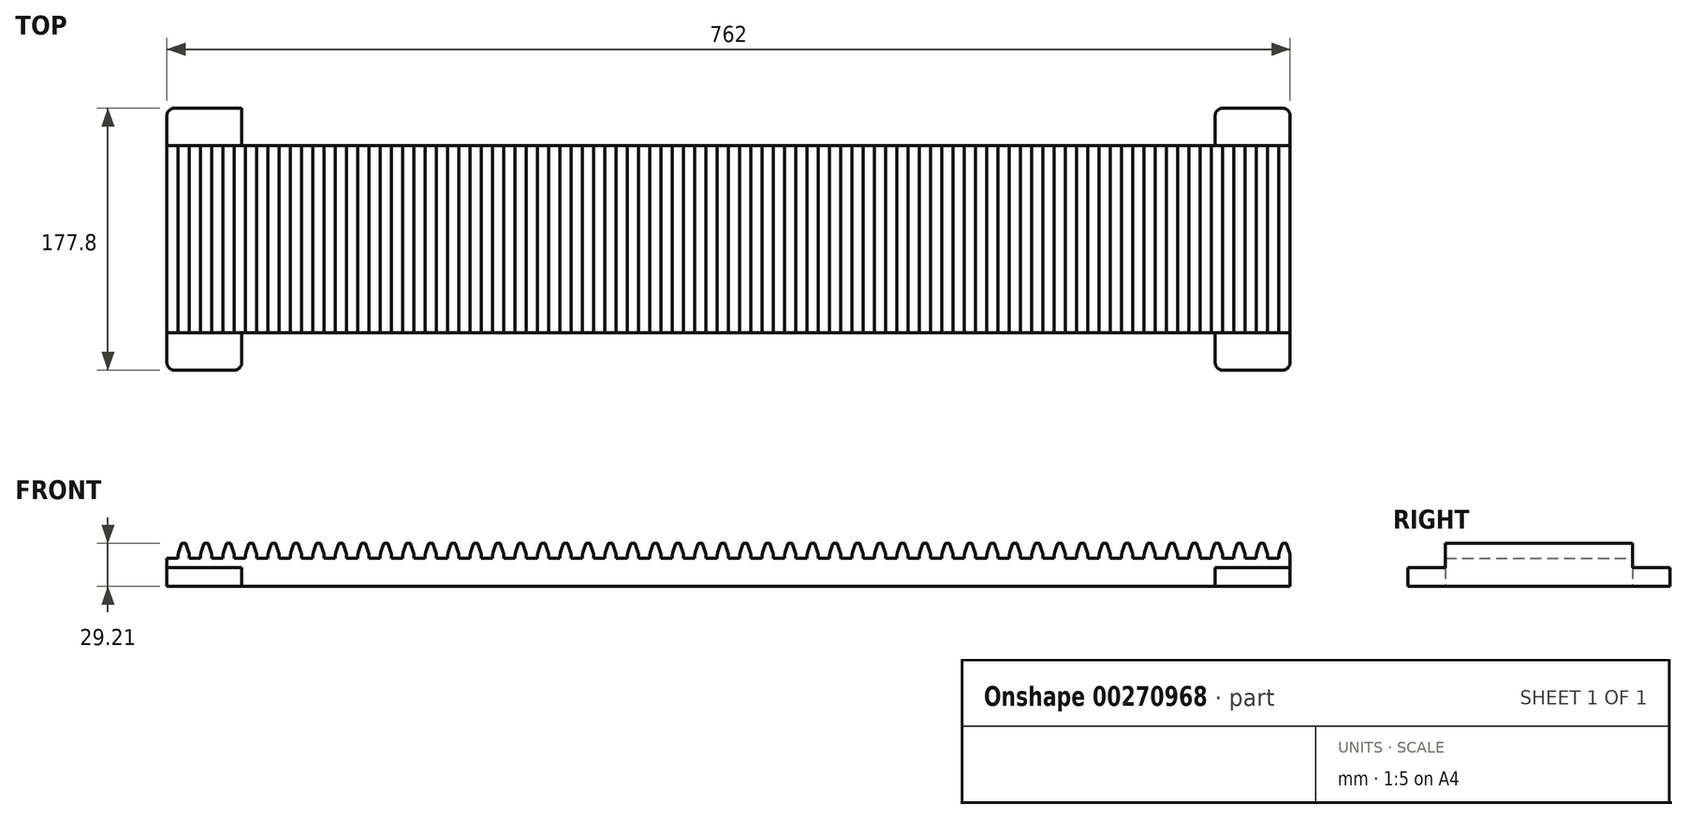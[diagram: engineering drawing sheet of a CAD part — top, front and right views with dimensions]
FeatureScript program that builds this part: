
annotation { "Feature Type Name" : "Feature", "Feature Type Description" : "" }
export const myFeature = defineFeature(function(context is Context, id is Id, definition is map)
    precondition{}
    {
        {
            var Q0;
            Q0=qCreatedBy(makeId("Front.planeOp"),FACE);
            var sketch = newSketch(context, id + "F0", { "sketchPlane" : qUnion([Q0])});
            skLineSegment(sketch, "E0", {"start": v(0, 0) * mm, "end": v(0, -19.05) * mm});
            skLineSegment(sketch, "E1", {"start": v(0, -19.05) * mm, "end": v(762, -19.05) * mm});
            skLineSegment(sketch, "E2", {"start": v(762, -19.05) * mm, "end": v(762, 0) * mm});
            skLineSegment(sketch, "E3", {"start": v(762, 0) * mm, "end": v(0, 0) * mm});
            skLineSegment(sketch, "E4", {"start": v(0, 0) * mm, "end": v(7.62, 0) * mm});
            skLineSegment(sketch, "E5", {"start": v(7.62, 0) * mm, "end": v(7.62, 1.79) * mm});
            skLineSegment(sketch, "E6", {"start": v(10.53, 10.16) * mm, "end": v(12.33, 10.16) * mm});
            skLineSegment(sketch, "E7", {"start": v(15.24, 1.79) * mm, "end": v(15.24, 0) * mm});
            skLineSegment(sketch, "E8", {"start": v(9.78, 9.6) * mm, "end": v(7.92, 3.7) * mm});
            skLineSegment(sketch, "E9", {"start": v(13.08, 9.6) * mm, "end": v(14.94, 3.7) * mm});
            skPoint(sketch, "E10.visualSharp", {"position": v(7.62, 2.77) * mm});
            skArc(sketch, "E10.filletArc", {"start": v(7.92, 3.7) * mm, "mid": v(7.7, 2.76) * mm, "end": v(7.62, 1.79) * mm});
            skPoint(sketch, "E11.visualSharp", {"position": v(15.24, 2.77) * mm});
            skArc(sketch, "E11.filletArc", {"start": v(15.24, 1.79) * mm, "mid": v(15.17, 2.76) * mm, "end": v(14.94, 3.7) * mm});
            skPoint(sketch, "E12.visualSharp", {"position": v(12.9, 10.16) * mm});
            skArc(sketch, "E12.filletArc", {"start": v(13.08, 9.6) * mm, "mid": v(12.8, 10) * mm, "end": v(12.33, 10.16) * mm});
            skPoint(sketch, "E13.visualSharp", {"position": v(9.96, 10.16) * mm});
            skArc(sketch, "E13.filletArc", {"start": v(10.53, 10.16) * mm, "mid": v(10.07, 10) * mm, "end": v(9.78, 9.6) * mm});
            skLineSegment(sketch, "E14", {"start": v(15.24, 0) * mm, "end": v(22.86, 0) * mm});
            skLineSegment(sketch, "E15.1.0.0", {"start": v(22.86, 0) * mm, "end": v(22.86, 1.79) * mm});
            skArc(sketch, "E15.1.0.1", {"start": v(23.16, 3.7) * mm, "mid": v(22.93, 2.76) * mm, "end": v(22.86, 1.79) * mm});
            skLineSegment(sketch, "E15.1.0.2", {"start": v(25.02, 9.6) * mm, "end": v(23.16, 3.7) * mm});
            skArc(sketch, "E15.1.0.3", {"start": v(25.77, 10.16) * mm, "mid": v(25.3, 10) * mm, "end": v(25.02, 9.6) * mm});
            skLineSegment(sketch, "E15.1.0.4", {"start": v(25.77, 10.16) * mm, "end": v(27.57, 10.16) * mm});
            skArc(sketch, "E15.1.0.5", {"start": v(28.32, 9.6) * mm, "mid": v(28.03, 10) * mm, "end": v(27.57, 10.16) * mm});
            skLineSegment(sketch, "E15.1.0.6", {"start": v(28.32, 9.6) * mm, "end": v(30.18, 3.7) * mm});
            skArc(sketch, "E15.1.0.7", {"start": v(30.48, 1.79) * mm, "mid": v(30.4, 2.76) * mm, "end": v(30.18, 3.7) * mm});
            skLineSegment(sketch, "E15.1.0.8", {"start": v(30.48, 1.79) * mm, "end": v(30.48, 0) * mm});
            skLineSegment(sketch, "E15.2.0.0", {"start": v(38.1, 0) * mm, "end": v(38.1, 1.79) * mm});
            skArc(sketch, "E15.2.0.1", {"start": v(38.4, 3.7) * mm, "mid": v(38.17, 2.76) * mm, "end": v(38.1, 1.79) * mm});
            skLineSegment(sketch, "E15.2.0.2", {"start": v(40.26, 9.6) * mm, "end": v(38.4, 3.7) * mm});
            skArc(sketch, "E15.2.0.3", {"start": v(41.01, 10.16) * mm, "mid": v(40.55, 10) * mm, "end": v(40.26, 9.6) * mm});
            skLineSegment(sketch, "E15.2.0.4", {"start": v(41.01, 10.16) * mm, "end": v(42.8, 10.16) * mm});
            skArc(sketch, "E15.2.0.5", {"start": v(43.56, 9.6) * mm, "mid": v(43.27, 10) * mm, "end": v(42.8, 10.16) * mm});
            skLineSegment(sketch, "E15.2.0.6", {"start": v(43.56, 9.6) * mm, "end": v(45.42, 3.7) * mm});
            skArc(sketch, "E15.2.0.7", {"start": v(45.72, 1.79) * mm, "mid": v(45.65, 2.76) * mm, "end": v(45.42, 3.7) * mm});
            skLineSegment(sketch, "E15.2.0.8", {"start": v(45.72, 1.79) * mm, "end": v(45.72, 0) * mm});
            skLineSegment(sketch, "E15.direction1", {"start": v(7.62, 0) * mm, "end": v(22.86, 0) * mm, "construction": true});
            skLineSegment(sketch, "E16.0.3.0", {"start": v(53.34, 0) * mm, "end": v(53.34, 1.79) * mm});
            skArc(sketch, "E16.3.3.0", {"start": v(53.64, 3.7) * mm, "mid": v(53.41, 2.76) * mm, "end": v(53.34, 1.79) * mm});
            skLineSegment(sketch, "E16.7.3.0", {"start": v(55.5, 9.6) * mm, "end": v(53.64, 3.7) * mm});
            skArc(sketch, "E16.10.3.0", {"start": v(56.25, 10.16) * mm, "mid": v(55.79, 10) * mm, "end": v(55.5, 9.6) * mm});
            skLineSegment(sketch, "E16.14.3.0", {"start": v(56.25, 10.16) * mm, "end": v(58.05, 10.16) * mm});
            skArc(sketch, "E16.17.3.0", {"start": v(58.8, 9.6) * mm, "mid": v(58.51, 10) * mm, "end": v(58.05, 10.16) * mm});
            skLineSegment(sketch, "E16.21.3.0", {"start": v(58.8, 9.6) * mm, "end": v(60.66, 3.7) * mm});
            skArc(sketch, "E16.24.3.0", {"start": v(60.96, 1.79) * mm, "mid": v(60.89, 2.76) * mm, "end": v(60.66, 3.7) * mm});
            skLineSegment(sketch, "E16.28.3.0", {"start": v(60.96, 1.79) * mm, "end": v(60.96, 0) * mm});
            skLineSegment(sketch, "E16.0.4.0", {"start": v(68.58, 0) * mm, "end": v(68.58, 1.79) * mm});
            skArc(sketch, "E16.3.4.0", {"start": v(68.88, 3.7) * mm, "mid": v(68.65, 2.76) * mm, "end": v(68.58, 1.79) * mm});
            skLineSegment(sketch, "E16.7.4.0", {"start": v(70.74, 9.6) * mm, "end": v(68.88, 3.7) * mm});
            skArc(sketch, "E16.10.4.0", {"start": v(71.5, 10.16) * mm, "mid": v(71.03, 10) * mm, "end": v(70.74, 9.6) * mm});
            skLineSegment(sketch, "E16.14.4.0", {"start": v(71.5, 10.16) * mm, "end": v(73.29, 10.16) * mm});
            skArc(sketch, "E16.17.4.0", {"start": v(74.04, 9.6) * mm, "mid": v(73.75, 10) * mm, "end": v(73.29, 10.16) * mm});
            skLineSegment(sketch, "E16.21.4.0", {"start": v(74.04, 9.6) * mm, "end": v(75.9, 3.7) * mm});
            skArc(sketch, "E16.24.4.0", {"start": v(76.2, 1.79) * mm, "mid": v(76.13, 2.76) * mm, "end": v(75.9, 3.7) * mm});
            skLineSegment(sketch, "E16.28.4.0", {"start": v(76.2, 1.79) * mm, "end": v(76.2, 0) * mm});
            skLineSegment(sketch, "E16.0.5.0", {"start": v(83.82, 0) * mm, "end": v(83.82, 1.79) * mm});
            skArc(sketch, "E16.3.5.0", {"start": v(84.12, 3.7) * mm, "mid": v(83.9, 2.76) * mm, "end": v(83.82, 1.79) * mm});
            skLineSegment(sketch, "E16.7.5.0", {"start": v(85.98, 9.6) * mm, "end": v(84.12, 3.7) * mm});
            skArc(sketch, "E16.10.5.0", {"start": v(86.73, 10.16) * mm, "mid": v(86.27, 10) * mm, "end": v(85.98, 9.6) * mm});
            skLineSegment(sketch, "E16.14.5.0", {"start": v(86.73, 10.16) * mm, "end": v(88.53, 10.16) * mm});
            skArc(sketch, "E16.17.5.0", {"start": v(89.28, 9.6) * mm, "mid": v(89, 10) * mm, "end": v(88.53, 10.16) * mm});
            skLineSegment(sketch, "E16.21.5.0", {"start": v(89.28, 9.6) * mm, "end": v(91.14, 3.7) * mm});
            skArc(sketch, "E16.24.5.0", {"start": v(91.44, 1.79) * mm, "mid": v(91.37, 2.76) * mm, "end": v(91.14, 3.7) * mm});
            skLineSegment(sketch, "E16.28.5.0", {"start": v(91.44, 1.79) * mm, "end": v(91.44, 0) * mm});
            skLineSegment(sketch, "E16.0.6.0", {"start": v(99.06, 0) * mm, "end": v(99.06, 1.79) * mm});
            skArc(sketch, "E16.3.6.0", {"start": v(99.36, 3.7) * mm, "mid": v(99.13, 2.76) * mm, "end": v(99.06, 1.79) * mm});
            skLineSegment(sketch, "E16.7.6.0", {"start": v(101.22, 9.6) * mm, "end": v(99.36, 3.7) * mm});
            skArc(sketch, "E16.10.6.0", {"start": v(101.97, 10.16) * mm, "mid": v(101.5, 10) * mm, "end": v(101.22, 9.6) * mm});
            skLineSegment(sketch, "E16.14.6.0", {"start": v(101.97, 10.16) * mm, "end": v(103.77, 10.16) * mm});
            skArc(sketch, "E16.17.6.0", {"start": v(104.52, 9.6) * mm, "mid": v(104.23, 10) * mm, "end": v(103.77, 10.16) * mm});
            skLineSegment(sketch, "E16.21.6.0", {"start": v(104.52, 9.6) * mm, "end": v(106.38, 3.7) * mm});
            skArc(sketch, "E16.24.6.0", {"start": v(106.68, 1.79) * mm, "mid": v(106.6, 2.76) * mm, "end": v(106.38, 3.7) * mm});
            skLineSegment(sketch, "E16.28.6.0", {"start": v(106.68, 1.79) * mm, "end": v(106.68, 0) * mm});
            skLineSegment(sketch, "E16.0.7.0", {"start": v(114.3, 0) * mm, "end": v(114.3, 1.79) * mm});
            skArc(sketch, "E16.3.7.0", {"start": v(114.6, 3.7) * mm, "mid": v(114.37, 2.76) * mm, "end": v(114.3, 1.79) * mm});
            skLineSegment(sketch, "E16.7.7.0", {"start": v(116.46, 9.6) * mm, "end": v(114.6, 3.7) * mm});
            skArc(sketch, "E16.10.7.0", {"start": v(117.21, 10.16) * mm, "mid": v(116.75, 10) * mm, "end": v(116.46, 9.6) * mm});
            skLineSegment(sketch, "E16.14.7.0", {"start": v(117.21, 10.16) * mm, "end": v(119, 10.16) * mm});
            skArc(sketch, "E16.17.7.0", {"start": v(119.76, 9.6) * mm, "mid": v(119.47, 10) * mm, "end": v(119, 10.16) * mm});
            skLineSegment(sketch, "E16.21.7.0", {"start": v(119.76, 9.6) * mm, "end": v(121.62, 3.7) * mm});
            skArc(sketch, "E16.24.7.0", {"start": v(121.92, 1.79) * mm, "mid": v(121.85, 2.76) * mm, "end": v(121.62, 3.7) * mm});
            skLineSegment(sketch, "E16.28.7.0", {"start": v(121.92, 1.79) * mm, "end": v(121.92, 0) * mm});
            skLineSegment(sketch, "E16.0.8.0", {"start": v(129.54, 0) * mm, "end": v(129.54, 1.79) * mm});
            skArc(sketch, "E16.3.8.0", {"start": v(129.84, 3.7) * mm, "mid": v(129.61, 2.76) * mm, "end": v(129.54, 1.79) * mm});
            skLineSegment(sketch, "E16.7.8.0", {"start": v(131.7, 9.6) * mm, "end": v(129.84, 3.7) * mm});
            skArc(sketch, "E16.10.8.0", {"start": v(132.45, 10.16) * mm, "mid": v(131.99, 10) * mm, "end": v(131.7, 9.6) * mm});
            skLineSegment(sketch, "E16.14.8.0", {"start": v(132.45, 10.16) * mm, "end": v(134.25, 10.16) * mm});
            skArc(sketch, "E16.17.8.0", {"start": v(135, 9.6) * mm, "mid": v(134.71, 10) * mm, "end": v(134.25, 10.16) * mm});
            skLineSegment(sketch, "E16.21.8.0", {"start": v(135, 9.6) * mm, "end": v(136.86, 3.7) * mm});
            skArc(sketch, "E16.24.8.0", {"start": v(137.16, 1.79) * mm, "mid": v(137.09, 2.76) * mm, "end": v(136.86, 3.7) * mm});
            skLineSegment(sketch, "E16.28.8.0", {"start": v(137.16, 1.79) * mm, "end": v(137.16, 0) * mm});
            skLineSegment(sketch, "E16.0.9.0", {"start": v(144.78, 0) * mm, "end": v(144.78, 1.79) * mm});
            skArc(sketch, "E16.3.9.0", {"start": v(145.08, 3.7) * mm, "mid": v(144.85, 2.76) * mm, "end": v(144.78, 1.79) * mm});
            skLineSegment(sketch, "E16.7.9.0", {"start": v(146.94, 9.6) * mm, "end": v(145.08, 3.7) * mm});
            skArc(sketch, "E16.10.9.0", {"start": v(147.7, 10.16) * mm, "mid": v(147.23, 10) * mm, "end": v(146.94, 9.6) * mm});
            skLineSegment(sketch, "E16.14.9.0", {"start": v(147.7, 10.16) * mm, "end": v(149.49, 10.16) * mm});
            skArc(sketch, "E16.17.9.0", {"start": v(150.24, 9.6) * mm, "mid": v(149.95, 10) * mm, "end": v(149.49, 10.16) * mm});
            skLineSegment(sketch, "E16.21.9.0", {"start": v(150.24, 9.6) * mm, "end": v(152.1, 3.7) * mm});
            skArc(sketch, "E16.24.9.0", {"start": v(152.4, 1.79) * mm, "mid": v(152.33, 2.76) * mm, "end": v(152.1, 3.7) * mm});
            skLineSegment(sketch, "E16.28.9.0", {"start": v(152.4, 1.79) * mm, "end": v(152.4, 0) * mm});
            skLineSegment(sketch, "E16.0.10.0", {"start": v(160.02, 0) * mm, "end": v(160.02, 1.79) * mm});
            skArc(sketch, "E16.3.10.0", {"start": v(160.32, 3.7) * mm, "mid": v(160.1, 2.76) * mm, "end": v(160.02, 1.79) * mm});
            skLineSegment(sketch, "E16.7.10.0", {"start": v(162.18, 9.6) * mm, "end": v(160.32, 3.7) * mm});
            skArc(sketch, "E16.10.10.0", {"start": v(162.93, 10.16) * mm, "mid": v(162.47, 10) * mm, "end": v(162.18, 9.6) * mm});
            skLineSegment(sketch, "E16.14.10.0", {"start": v(162.93, 10.16) * mm, "end": v(164.73, 10.16) * mm});
            skArc(sketch, "E16.17.10.0", {"start": v(165.48, 9.6) * mm, "mid": v(165.2, 10) * mm, "end": v(164.73, 10.16) * mm});
            skLineSegment(sketch, "E16.21.10.0", {"start": v(165.48, 9.6) * mm, "end": v(167.34, 3.7) * mm});
            skArc(sketch, "E16.24.10.0", {"start": v(167.64, 1.79) * mm, "mid": v(167.57, 2.76) * mm, "end": v(167.34, 3.7) * mm});
            skLineSegment(sketch, "E16.28.10.0", {"start": v(167.64, 1.79) * mm, "end": v(167.64, 0) * mm});
            skLineSegment(sketch, "E16.0.11.0", {"start": v(175.26, 0) * mm, "end": v(175.26, 1.79) * mm});
            skArc(sketch, "E16.3.11.0", {"start": v(175.56, 3.7) * mm, "mid": v(175.33, 2.76) * mm, "end": v(175.26, 1.79) * mm});
            skLineSegment(sketch, "E16.7.11.0", {"start": v(177.42, 9.6) * mm, "end": v(175.56, 3.7) * mm});
            skArc(sketch, "E16.10.11.0", {"start": v(178.17, 10.16) * mm, "mid": v(177.7, 10) * mm, "end": v(177.42, 9.6) * mm});
            skLineSegment(sketch, "E16.14.11.0", {"start": v(178.17, 10.16) * mm, "end": v(179.97, 10.16) * mm});
            skArc(sketch, "E16.17.11.0", {"start": v(180.72, 9.6) * mm, "mid": v(180.43, 10) * mm, "end": v(179.97, 10.16) * mm});
            skLineSegment(sketch, "E16.21.11.0", {"start": v(180.72, 9.6) * mm, "end": v(182.58, 3.7) * mm});
            skArc(sketch, "E16.24.11.0", {"start": v(182.88, 1.79) * mm, "mid": v(182.8, 2.76) * mm, "end": v(182.58, 3.7) * mm});
            skLineSegment(sketch, "E16.28.11.0", {"start": v(182.88, 1.79) * mm, "end": v(182.88, 0) * mm});
            skLineSegment(sketch, "E16.0.12.0", {"start": v(190.5, 0) * mm, "end": v(190.5, 1.79) * mm});
            skArc(sketch, "E16.3.12.0", {"start": v(190.8, 3.7) * mm, "mid": v(190.57, 2.76) * mm, "end": v(190.5, 1.79) * mm});
            skLineSegment(sketch, "E16.7.12.0", {"start": v(192.66, 9.6) * mm, "end": v(190.8, 3.7) * mm});
            skArc(sketch, "E16.10.12.0", {"start": v(193.41, 10.16) * mm, "mid": v(192.95, 10) * mm, "end": v(192.66, 9.6) * mm});
            skLineSegment(sketch, "E16.14.12.0", {"start": v(193.41, 10.16) * mm, "end": v(195.2, 10.16) * mm});
            skArc(sketch, "E16.17.12.0", {"start": v(195.96, 9.6) * mm, "mid": v(195.67, 10) * mm, "end": v(195.2, 10.16) * mm});
            skLineSegment(sketch, "E16.21.12.0", {"start": v(195.96, 9.6) * mm, "end": v(197.82, 3.7) * mm});
            skArc(sketch, "E16.24.12.0", {"start": v(198.12, 1.79) * mm, "mid": v(198.05, 2.76) * mm, "end": v(197.82, 3.7) * mm});
            skLineSegment(sketch, "E16.28.12.0", {"start": v(198.12, 1.79) * mm, "end": v(198.12, 0) * mm});
            skLineSegment(sketch, "E16.0.13.0", {"start": v(205.74, 0) * mm, "end": v(205.74, 1.79) * mm});
            skArc(sketch, "E16.3.13.0", {"start": v(206.04, 3.7) * mm, "mid": v(205.81, 2.76) * mm, "end": v(205.74, 1.79) * mm});
            skLineSegment(sketch, "E16.7.13.0", {"start": v(207.9, 9.6) * mm, "end": v(206.04, 3.7) * mm});
            skArc(sketch, "E16.10.13.0", {"start": v(208.65, 10.16) * mm, "mid": v(208.19, 10) * mm, "end": v(207.9, 9.6) * mm});
            skLineSegment(sketch, "E16.14.13.0", {"start": v(208.65, 10.16) * mm, "end": v(210.45, 10.16) * mm});
            skArc(sketch, "E16.17.13.0", {"start": v(211.2, 9.6) * mm, "mid": v(210.91, 10) * mm, "end": v(210.45, 10.16) * mm});
            skLineSegment(sketch, "E16.21.13.0", {"start": v(211.2, 9.6) * mm, "end": v(213.06, 3.7) * mm});
            skArc(sketch, "E16.24.13.0", {"start": v(213.36, 1.79) * mm, "mid": v(213.29, 2.76) * mm, "end": v(213.06, 3.7) * mm});
            skLineSegment(sketch, "E16.28.13.0", {"start": v(213.36, 1.79) * mm, "end": v(213.36, 0) * mm});
            skLineSegment(sketch, "E16.0.14.0", {"start": v(220.98, 0) * mm, "end": v(220.98, 1.79) * mm});
            skArc(sketch, "E16.3.14.0", {"start": v(221.28, 3.7) * mm, "mid": v(221.05, 2.76) * mm, "end": v(220.98, 1.79) * mm});
            skLineSegment(sketch, "E16.7.14.0", {"start": v(223.14, 9.6) * mm, "end": v(221.28, 3.7) * mm});
            skArc(sketch, "E16.10.14.0", {"start": v(223.9, 10.16) * mm, "mid": v(223.43, 10) * mm, "end": v(223.14, 9.6) * mm});
            skLineSegment(sketch, "E16.14.14.0", {"start": v(223.9, 10.16) * mm, "end": v(225.69, 10.16) * mm});
            skArc(sketch, "E16.17.14.0", {"start": v(226.44, 9.6) * mm, "mid": v(226.15, 10) * mm, "end": v(225.69, 10.16) * mm});
            skLineSegment(sketch, "E16.21.14.0", {"start": v(226.44, 9.6) * mm, "end": v(228.3, 3.7) * mm});
            skArc(sketch, "E16.24.14.0", {"start": v(228.6, 1.79) * mm, "mid": v(228.53, 2.76) * mm, "end": v(228.3, 3.7) * mm});
            skLineSegment(sketch, "E16.28.14.0", {"start": v(228.6, 1.79) * mm, "end": v(228.6, 0) * mm});
            skLineSegment(sketch, "E16.0.15.0", {"start": v(236.22, 0) * mm, "end": v(236.22, 1.79) * mm});
            skArc(sketch, "E16.3.15.0", {"start": v(236.52, 3.7) * mm, "mid": v(236.3, 2.76) * mm, "end": v(236.22, 1.79) * mm});
            skLineSegment(sketch, "E16.7.15.0", {"start": v(238.38, 9.6) * mm, "end": v(236.52, 3.7) * mm});
            skArc(sketch, "E16.10.15.0", {"start": v(239.13, 10.16) * mm, "mid": v(238.67, 10) * mm, "end": v(238.38, 9.6) * mm});
            skLineSegment(sketch, "E16.14.15.0", {"start": v(239.13, 10.16) * mm, "end": v(240.93, 10.16) * mm});
            skArc(sketch, "E16.17.15.0", {"start": v(241.68, 9.6) * mm, "mid": v(241.4, 10) * mm, "end": v(240.93, 10.16) * mm});
            skLineSegment(sketch, "E16.21.15.0", {"start": v(241.68, 9.6) * mm, "end": v(243.54, 3.7) * mm});
            skArc(sketch, "E16.24.15.0", {"start": v(243.84, 1.79) * mm, "mid": v(243.77, 2.76) * mm, "end": v(243.54, 3.7) * mm});
            skLineSegment(sketch, "E16.28.15.0", {"start": v(243.84, 1.79) * mm, "end": v(243.84, 0) * mm});
            skLineSegment(sketch, "E16.0.16.0", {"start": v(251.46, 0) * mm, "end": v(251.46, 1.79) * mm});
            skArc(sketch, "E16.3.16.0", {"start": v(251.76, 3.7) * mm, "mid": v(251.53, 2.76) * mm, "end": v(251.46, 1.79) * mm});
            skLineSegment(sketch, "E16.7.16.0", {"start": v(253.62, 9.6) * mm, "end": v(251.76, 3.7) * mm});
            skArc(sketch, "E16.10.16.0", {"start": v(254.37, 10.16) * mm, "mid": v(253.9, 10) * mm, "end": v(253.62, 9.6) * mm});
            skLineSegment(sketch, "E16.14.16.0", {"start": v(254.37, 10.16) * mm, "end": v(256.17, 10.16) * mm});
            skArc(sketch, "E16.17.16.0", {"start": v(256.92, 9.6) * mm, "mid": v(256.63, 10) * mm, "end": v(256.17, 10.16) * mm});
            skLineSegment(sketch, "E16.21.16.0", {"start": v(256.92, 9.6) * mm, "end": v(258.78, 3.7) * mm});
            skArc(sketch, "E16.24.16.0", {"start": v(259.08, 1.79) * mm, "mid": v(259, 2.76) * mm, "end": v(258.78, 3.7) * mm});
            skLineSegment(sketch, "E16.28.16.0", {"start": v(259.08, 1.79) * mm, "end": v(259.08, 0) * mm});
            skLineSegment(sketch, "E16.0.17.0", {"start": v(266.7, 0) * mm, "end": v(266.7, 1.79) * mm});
            skArc(sketch, "E16.3.17.0", {"start": v(267, 3.7) * mm, "mid": v(266.77, 2.76) * mm, "end": v(266.7, 1.79) * mm});
            skLineSegment(sketch, "E16.7.17.0", {"start": v(268.86, 9.6) * mm, "end": v(267, 3.7) * mm});
            skArc(sketch, "E16.10.17.0", {"start": v(269.61, 10.16) * mm, "mid": v(269.15, 10) * mm, "end": v(268.86, 9.6) * mm});
            skLineSegment(sketch, "E16.14.17.0", {"start": v(269.61, 10.16) * mm, "end": v(271.4, 10.16) * mm});
            skArc(sketch, "E16.17.17.0", {"start": v(272.16, 9.6) * mm, "mid": v(271.87, 10) * mm, "end": v(271.4, 10.16) * mm});
            skLineSegment(sketch, "E16.21.17.0", {"start": v(272.16, 9.6) * mm, "end": v(274.02, 3.7) * mm});
            skArc(sketch, "E16.24.17.0", {"start": v(274.32, 1.79) * mm, "mid": v(274.25, 2.76) * mm, "end": v(274.02, 3.7) * mm});
            skLineSegment(sketch, "E16.28.17.0", {"start": v(274.32, 1.79) * mm, "end": v(274.32, 0) * mm});
            skLineSegment(sketch, "E16.0.18.0", {"start": v(281.94, 0) * mm, "end": v(281.94, 1.79) * mm});
            skArc(sketch, "E16.3.18.0", {"start": v(282.24, 3.7) * mm, "mid": v(282.01, 2.76) * mm, "end": v(281.94, 1.79) * mm});
            skLineSegment(sketch, "E16.7.18.0", {"start": v(284.1, 9.6) * mm, "end": v(282.24, 3.7) * mm});
            skArc(sketch, "E16.10.18.0", {"start": v(284.85, 10.16) * mm, "mid": v(284.39, 10) * mm, "end": v(284.1, 9.6) * mm});
            skLineSegment(sketch, "E16.14.18.0", {"start": v(284.85, 10.16) * mm, "end": v(286.65, 10.16) * mm});
            skArc(sketch, "E16.17.18.0", {"start": v(287.4, 9.6) * mm, "mid": v(287.11, 10) * mm, "end": v(286.65, 10.16) * mm});
            skLineSegment(sketch, "E16.21.18.0", {"start": v(287.4, 9.6) * mm, "end": v(289.26, 3.7) * mm});
            skArc(sketch, "E16.24.18.0", {"start": v(289.56, 1.79) * mm, "mid": v(289.49, 2.76) * mm, "end": v(289.26, 3.7) * mm});
            skLineSegment(sketch, "E16.28.18.0", {"start": v(289.56, 1.79) * mm, "end": v(289.56, 0) * mm});
            skLineSegment(sketch, "E16.0.19.0", {"start": v(297.18, 0) * mm, "end": v(297.18, 1.79) * mm});
            skArc(sketch, "E16.3.19.0", {"start": v(297.48, 3.7) * mm, "mid": v(297.25, 2.76) * mm, "end": v(297.18, 1.79) * mm});
            skLineSegment(sketch, "E16.7.19.0", {"start": v(299.34, 9.6) * mm, "end": v(297.48, 3.7) * mm});
            skArc(sketch, "E16.10.19.0", {"start": v(300.1, 10.16) * mm, "mid": v(299.63, 10) * mm, "end": v(299.34, 9.6) * mm});
            skLineSegment(sketch, "E16.14.19.0", {"start": v(300.1, 10.16) * mm, "end": v(301.89, 10.16) * mm});
            skArc(sketch, "E16.17.19.0", {"start": v(302.64, 9.6) * mm, "mid": v(302.35, 10) * mm, "end": v(301.89, 10.16) * mm});
            skLineSegment(sketch, "E16.21.19.0", {"start": v(302.64, 9.6) * mm, "end": v(304.5, 3.7) * mm});
            skArc(sketch, "E16.24.19.0", {"start": v(304.8, 1.79) * mm, "mid": v(304.73, 2.76) * mm, "end": v(304.5, 3.7) * mm});
            skLineSegment(sketch, "E16.28.19.0", {"start": v(304.8, 1.79) * mm, "end": v(304.8, 0) * mm});
            skLineSegment(sketch, "E16.0.20.0", {"start": v(312.42, 0) * mm, "end": v(312.42, 1.79) * mm});
            skArc(sketch, "E16.3.20.0", {"start": v(312.72, 3.7) * mm, "mid": v(312.5, 2.76) * mm, "end": v(312.42, 1.79) * mm});
            skLineSegment(sketch, "E16.7.20.0", {"start": v(314.58, 9.6) * mm, "end": v(312.72, 3.7) * mm});
            skArc(sketch, "E16.10.20.0", {"start": v(315.33, 10.16) * mm, "mid": v(314.87, 10) * mm, "end": v(314.58, 9.6) * mm});
            skLineSegment(sketch, "E16.14.20.0", {"start": v(315.33, 10.16) * mm, "end": v(317.13, 10.16) * mm});
            skArc(sketch, "E16.17.20.0", {"start": v(317.88, 9.6) * mm, "mid": v(317.6, 10) * mm, "end": v(317.13, 10.16) * mm});
            skLineSegment(sketch, "E16.21.20.0", {"start": v(317.88, 9.6) * mm, "end": v(319.74, 3.7) * mm});
            skArc(sketch, "E16.24.20.0", {"start": v(320.04, 1.79) * mm, "mid": v(319.97, 2.76) * mm, "end": v(319.74, 3.7) * mm});
            skLineSegment(sketch, "E16.28.20.0", {"start": v(320.04, 1.79) * mm, "end": v(320.04, 0) * mm});
            skLineSegment(sketch, "E16.0.21.0", {"start": v(327.66, 0) * mm, "end": v(327.66, 1.79) * mm});
            skArc(sketch, "E16.3.21.0", {"start": v(327.96, 3.7) * mm, "mid": v(327.73, 2.76) * mm, "end": v(327.66, 1.79) * mm});
            skLineSegment(sketch, "E16.7.21.0", {"start": v(329.82, 9.6) * mm, "end": v(327.96, 3.7) * mm});
            skArc(sketch, "E16.10.21.0", {"start": v(330.57, 10.16) * mm, "mid": v(330.1, 10) * mm, "end": v(329.82, 9.6) * mm});
            skLineSegment(sketch, "E16.14.21.0", {"start": v(330.57, 10.16) * mm, "end": v(332.37, 10.16) * mm});
            skArc(sketch, "E16.17.21.0", {"start": v(333.12, 9.6) * mm, "mid": v(332.83, 10) * mm, "end": v(332.37, 10.16) * mm});
            skLineSegment(sketch, "E16.21.21.0", {"start": v(333.12, 9.6) * mm, "end": v(334.98, 3.7) * mm});
            skArc(sketch, "E16.24.21.0", {"start": v(335.28, 1.79) * mm, "mid": v(335.2, 2.76) * mm, "end": v(334.98, 3.7) * mm});
            skLineSegment(sketch, "E16.28.21.0", {"start": v(335.28, 1.79) * mm, "end": v(335.28, 0) * mm});
            skLineSegment(sketch, "E16.0.22.0", {"start": v(342.9, 0) * mm, "end": v(342.9, 1.79) * mm});
            skArc(sketch, "E16.3.22.0", {"start": v(343.2, 3.7) * mm, "mid": v(342.97, 2.76) * mm, "end": v(342.9, 1.79) * mm});
            skLineSegment(sketch, "E16.7.22.0", {"start": v(345.06, 9.6) * mm, "end": v(343.2, 3.7) * mm});
            skArc(sketch, "E16.10.22.0", {"start": v(345.81, 10.16) * mm, "mid": v(345.35, 10) * mm, "end": v(345.06, 9.6) * mm});
            skLineSegment(sketch, "E16.14.22.0", {"start": v(345.81, 10.16) * mm, "end": v(347.6, 10.16) * mm});
            skArc(sketch, "E16.17.22.0", {"start": v(348.36, 9.6) * mm, "mid": v(348.07, 10) * mm, "end": v(347.6, 10.16) * mm});
            skLineSegment(sketch, "E16.21.22.0", {"start": v(348.36, 9.6) * mm, "end": v(350.22, 3.7) * mm});
            skArc(sketch, "E16.24.22.0", {"start": v(350.52, 1.79) * mm, "mid": v(350.45, 2.76) * mm, "end": v(350.22, 3.7) * mm});
            skLineSegment(sketch, "E16.28.22.0", {"start": v(350.52, 1.79) * mm, "end": v(350.52, 0) * mm});
            skLineSegment(sketch, "E16.0.23.0", {"start": v(358.14, 0) * mm, "end": v(358.14, 1.79) * mm});
            skArc(sketch, "E16.3.23.0", {"start": v(358.44, 3.7) * mm, "mid": v(358.21, 2.76) * mm, "end": v(358.14, 1.79) * mm});
            skLineSegment(sketch, "E16.7.23.0", {"start": v(360.3, 9.6) * mm, "end": v(358.44, 3.7) * mm});
            skArc(sketch, "E16.10.23.0", {"start": v(361.05, 10.16) * mm, "mid": v(360.59, 10) * mm, "end": v(360.3, 9.6) * mm});
            skLineSegment(sketch, "E16.14.23.0", {"start": v(361.05, 10.16) * mm, "end": v(362.85, 10.16) * mm});
            skArc(sketch, "E16.17.23.0", {"start": v(363.6, 9.6) * mm, "mid": v(363.31, 10) * mm, "end": v(362.85, 10.16) * mm});
            skLineSegment(sketch, "E16.21.23.0", {"start": v(363.6, 9.6) * mm, "end": v(365.46, 3.7) * mm});
            skArc(sketch, "E16.24.23.0", {"start": v(365.76, 1.79) * mm, "mid": v(365.69, 2.76) * mm, "end": v(365.46, 3.7) * mm});
            skLineSegment(sketch, "E16.28.23.0", {"start": v(365.76, 1.79) * mm, "end": v(365.76, 0) * mm});
            skLineSegment(sketch, "E16.0.24.0", {"start": v(373.38, 0) * mm, "end": v(373.38, 1.79) * mm});
            skArc(sketch, "E16.3.24.0", {"start": v(373.68, 3.7) * mm, "mid": v(373.45, 2.76) * mm, "end": v(373.38, 1.79) * mm});
            skLineSegment(sketch, "E16.7.24.0", {"start": v(375.54, 9.6) * mm, "end": v(373.68, 3.7) * mm});
            skArc(sketch, "E16.10.24.0", {"start": v(376.3, 10.16) * mm, "mid": v(375.83, 10) * mm, "end": v(375.54, 9.6) * mm});
            skLineSegment(sketch, "E16.14.24.0", {"start": v(376.3, 10.16) * mm, "end": v(378.09, 10.16) * mm});
            skArc(sketch, "E16.17.24.0", {"start": v(378.84, 9.6) * mm, "mid": v(378.55, 10) * mm, "end": v(378.09, 10.16) * mm});
            skLineSegment(sketch, "E16.21.24.0", {"start": v(378.84, 9.6) * mm, "end": v(380.7, 3.7) * mm});
            skArc(sketch, "E16.24.24.0", {"start": v(381, 1.79) * mm, "mid": v(380.93, 2.76) * mm, "end": v(380.7, 3.7) * mm});
            skLineSegment(sketch, "E16.28.24.0", {"start": v(381, 1.79) * mm, "end": v(381, 0) * mm});
            skLineSegment(sketch, "E16.0.25.0", {"start": v(388.62, 0) * mm, "end": v(388.62, 1.79) * mm});
            skArc(sketch, "E16.3.25.0", {"start": v(388.92, 3.7) * mm, "mid": v(388.7, 2.76) * mm, "end": v(388.62, 1.79) * mm});
            skLineSegment(sketch, "E16.7.25.0", {"start": v(390.78, 9.6) * mm, "end": v(388.92, 3.7) * mm});
            skArc(sketch, "E16.10.25.0", {"start": v(391.53, 10.16) * mm, "mid": v(391.07, 10) * mm, "end": v(390.78, 9.6) * mm});
            skLineSegment(sketch, "E16.14.25.0", {"start": v(391.53, 10.16) * mm, "end": v(393.33, 10.16) * mm});
            skArc(sketch, "E16.17.25.0", {"start": v(394.08, 9.6) * mm, "mid": v(393.8, 10) * mm, "end": v(393.33, 10.16) * mm});
            skLineSegment(sketch, "E16.21.25.0", {"start": v(394.08, 9.6) * mm, "end": v(395.94, 3.7) * mm});
            skArc(sketch, "E16.24.25.0", {"start": v(396.24, 1.79) * mm, "mid": v(396.17, 2.76) * mm, "end": v(395.94, 3.7) * mm});
            skLineSegment(sketch, "E16.28.25.0", {"start": v(396.24, 1.79) * mm, "end": v(396.24, 0) * mm});
            skLineSegment(sketch, "E16.0.26.0", {"start": v(403.86, 0) * mm, "end": v(403.86, 1.79) * mm});
            skArc(sketch, "E16.3.26.0", {"start": v(404.16, 3.7) * mm, "mid": v(403.93, 2.76) * mm, "end": v(403.86, 1.79) * mm});
            skLineSegment(sketch, "E16.7.26.0", {"start": v(406.02, 9.6) * mm, "end": v(404.16, 3.7) * mm});
            skArc(sketch, "E16.10.26.0", {"start": v(406.77, 10.16) * mm, "mid": v(406.3, 10) * mm, "end": v(406.02, 9.6) * mm});
            skLineSegment(sketch, "E16.14.26.0", {"start": v(406.77, 10.16) * mm, "end": v(408.57, 10.16) * mm});
            skArc(sketch, "E16.17.26.0", {"start": v(409.32, 9.6) * mm, "mid": v(409.03, 10) * mm, "end": v(408.57, 10.16) * mm});
            skLineSegment(sketch, "E16.21.26.0", {"start": v(409.32, 9.6) * mm, "end": v(411.18, 3.7) * mm});
            skArc(sketch, "E16.24.26.0", {"start": v(411.48, 1.79) * mm, "mid": v(411.4, 2.76) * mm, "end": v(411.18, 3.7) * mm});
            skLineSegment(sketch, "E16.28.26.0", {"start": v(411.48, 1.79) * mm, "end": v(411.48, 0) * mm});
            skLineSegment(sketch, "E16.0.27.0", {"start": v(419.1, 0) * mm, "end": v(419.1, 1.79) * mm});
            skArc(sketch, "E16.3.27.0", {"start": v(419.4, 3.7) * mm, "mid": v(419.17, 2.76) * mm, "end": v(419.1, 1.79) * mm});
            skLineSegment(sketch, "E16.7.27.0", {"start": v(421.26, 9.6) * mm, "end": v(419.4, 3.7) * mm});
            skArc(sketch, "E16.10.27.0", {"start": v(422.01, 10.16) * mm, "mid": v(421.55, 10) * mm, "end": v(421.26, 9.6) * mm});
            skLineSegment(sketch, "E16.14.27.0", {"start": v(422.01, 10.16) * mm, "end": v(423.8, 10.16) * mm});
            skArc(sketch, "E16.17.27.0", {"start": v(424.56, 9.6) * mm, "mid": v(424.27, 10) * mm, "end": v(423.8, 10.16) * mm});
            skLineSegment(sketch, "E16.21.27.0", {"start": v(424.56, 9.6) * mm, "end": v(426.42, 3.7) * mm});
            skArc(sketch, "E16.24.27.0", {"start": v(426.72, 1.79) * mm, "mid": v(426.65, 2.76) * mm, "end": v(426.42, 3.7) * mm});
            skLineSegment(sketch, "E16.28.27.0", {"start": v(426.72, 1.79) * mm, "end": v(426.72, 0) * mm});
            skLineSegment(sketch, "E16.0.28.0", {"start": v(434.34, 0) * mm, "end": v(434.34, 1.79) * mm});
            skArc(sketch, "E16.3.28.0", {"start": v(434.64, 3.7) * mm, "mid": v(434.41, 2.76) * mm, "end": v(434.34, 1.79) * mm});
            skLineSegment(sketch, "E16.7.28.0", {"start": v(436.5, 9.6) * mm, "end": v(434.64, 3.7) * mm});
            skArc(sketch, "E16.10.28.0", {"start": v(437.25, 10.16) * mm, "mid": v(436.79, 10) * mm, "end": v(436.5, 9.6) * mm});
            skLineSegment(sketch, "E16.14.28.0", {"start": v(437.25, 10.16) * mm, "end": v(439.05, 10.16) * mm});
            skArc(sketch, "E16.17.28.0", {"start": v(439.8, 9.6) * mm, "mid": v(439.51, 10) * mm, "end": v(439.05, 10.16) * mm});
            skLineSegment(sketch, "E16.21.28.0", {"start": v(439.8, 9.6) * mm, "end": v(441.66, 3.7) * mm});
            skArc(sketch, "E16.24.28.0", {"start": v(441.96, 1.79) * mm, "mid": v(441.89, 2.76) * mm, "end": v(441.66, 3.7) * mm});
            skLineSegment(sketch, "E16.28.28.0", {"start": v(441.96, 1.79) * mm, "end": v(441.96, 0) * mm});
            skLineSegment(sketch, "E16.0.29.0", {"start": v(449.58, 0) * mm, "end": v(449.58, 1.79) * mm});
            skArc(sketch, "E16.3.29.0", {"start": v(449.88, 3.7) * mm, "mid": v(449.65, 2.76) * mm, "end": v(449.58, 1.79) * mm});
            skLineSegment(sketch, "E16.7.29.0", {"start": v(451.74, 9.6) * mm, "end": v(449.88, 3.7) * mm});
            skArc(sketch, "E16.10.29.0", {"start": v(452.5, 10.16) * mm, "mid": v(452.03, 10) * mm, "end": v(451.74, 9.6) * mm});
            skLineSegment(sketch, "E16.14.29.0", {"start": v(452.5, 10.16) * mm, "end": v(454.29, 10.16) * mm});
            skArc(sketch, "E16.17.29.0", {"start": v(455.04, 9.6) * mm, "mid": v(454.75, 10) * mm, "end": v(454.29, 10.16) * mm});
            skLineSegment(sketch, "E16.21.29.0", {"start": v(455.04, 9.6) * mm, "end": v(456.9, 3.7) * mm});
            skArc(sketch, "E16.24.29.0", {"start": v(457.2, 1.79) * mm, "mid": v(457.13, 2.76) * mm, "end": v(456.9, 3.7) * mm});
            skLineSegment(sketch, "E16.28.29.0", {"start": v(457.2, 1.79) * mm, "end": v(457.2, 0) * mm});
            skLineSegment(sketch, "E16.0.30.0", {"start": v(464.82, 0) * mm, "end": v(464.82, 1.79) * mm});
            skArc(sketch, "E16.3.30.0", {"start": v(465.12, 3.7) * mm, "mid": v(464.9, 2.76) * mm, "end": v(464.82, 1.79) * mm});
            skLineSegment(sketch, "E16.7.30.0", {"start": v(466.98, 9.6) * mm, "end": v(465.12, 3.7) * mm});
            skArc(sketch, "E16.10.30.0", {"start": v(467.73, 10.16) * mm, "mid": v(467.27, 10) * mm, "end": v(466.98, 9.6) * mm});
            skLineSegment(sketch, "E16.14.30.0", {"start": v(467.73, 10.16) * mm, "end": v(469.53, 10.16) * mm});
            skArc(sketch, "E16.17.30.0", {"start": v(470.28, 9.6) * mm, "mid": v(470, 10) * mm, "end": v(469.53, 10.16) * mm});
            skLineSegment(sketch, "E16.21.30.0", {"start": v(470.28, 9.6) * mm, "end": v(472.14, 3.7) * mm});
            skArc(sketch, "E16.24.30.0", {"start": v(472.44, 1.79) * mm, "mid": v(472.37, 2.76) * mm, "end": v(472.14, 3.7) * mm});
            skLineSegment(sketch, "E16.28.30.0", {"start": v(472.44, 1.79) * mm, "end": v(472.44, 0) * mm});
            skLineSegment(sketch, "E16.0.31.0", {"start": v(480.06, 0) * mm, "end": v(480.06, 1.79) * mm});
            skArc(sketch, "E16.3.31.0", {"start": v(480.36, 3.7) * mm, "mid": v(480.13, 2.76) * mm, "end": v(480.06, 1.79) * mm});
            skLineSegment(sketch, "E16.7.31.0", {"start": v(482.22, 9.6) * mm, "end": v(480.36, 3.7) * mm});
            skArc(sketch, "E16.10.31.0", {"start": v(482.97, 10.16) * mm, "mid": v(482.5, 10) * mm, "end": v(482.22, 9.6) * mm});
            skLineSegment(sketch, "E16.14.31.0", {"start": v(482.97, 10.16) * mm, "end": v(484.77, 10.16) * mm});
            skArc(sketch, "E16.17.31.0", {"start": v(485.52, 9.6) * mm, "mid": v(485.23, 10) * mm, "end": v(484.77, 10.16) * mm});
            skLineSegment(sketch, "E16.21.31.0", {"start": v(485.52, 9.6) * mm, "end": v(487.38, 3.7) * mm});
            skArc(sketch, "E16.24.31.0", {"start": v(487.68, 1.79) * mm, "mid": v(487.6, 2.76) * mm, "end": v(487.38, 3.7) * mm});
            skLineSegment(sketch, "E16.28.31.0", {"start": v(487.68, 1.79) * mm, "end": v(487.68, 0) * mm});
            skLineSegment(sketch, "E16.0.32.0", {"start": v(495.3, 0) * mm, "end": v(495.3, 1.79) * mm});
            skArc(sketch, "E16.3.32.0", {"start": v(495.6, 3.7) * mm, "mid": v(495.37, 2.76) * mm, "end": v(495.3, 1.79) * mm});
            skLineSegment(sketch, "E16.7.32.0", {"start": v(497.46, 9.6) * mm, "end": v(495.6, 3.7) * mm});
            skArc(sketch, "E16.10.32.0", {"start": v(498.21, 10.16) * mm, "mid": v(497.75, 10) * mm, "end": v(497.46, 9.6) * mm});
            skLineSegment(sketch, "E16.14.32.0", {"start": v(498.21, 10.16) * mm, "end": v(500, 10.16) * mm});
            skArc(sketch, "E16.17.32.0", {"start": v(500.76, 9.6) * mm, "mid": v(500.47, 10) * mm, "end": v(500, 10.16) * mm});
            skLineSegment(sketch, "E16.21.32.0", {"start": v(500.76, 9.6) * mm, "end": v(502.62, 3.7) * mm});
            skArc(sketch, "E16.24.32.0", {"start": v(502.92, 1.79) * mm, "mid": v(502.85, 2.76) * mm, "end": v(502.62, 3.7) * mm});
            skLineSegment(sketch, "E16.28.32.0", {"start": v(502.92, 1.79) * mm, "end": v(502.92, 0) * mm});
            skLineSegment(sketch, "E16.0.33.0", {"start": v(510.54, 0) * mm, "end": v(510.54, 1.79) * mm});
            skArc(sketch, "E16.3.33.0", {"start": v(510.84, 3.7) * mm, "mid": v(510.61, 2.76) * mm, "end": v(510.54, 1.79) * mm});
            skLineSegment(sketch, "E16.7.33.0", {"start": v(512.7, 9.6) * mm, "end": v(510.84, 3.7) * mm});
            skArc(sketch, "E16.10.33.0", {"start": v(513.45, 10.16) * mm, "mid": v(512.99, 10) * mm, "end": v(512.7, 9.6) * mm});
            skLineSegment(sketch, "E16.14.33.0", {"start": v(513.45, 10.16) * mm, "end": v(515.25, 10.16) * mm});
            skArc(sketch, "E16.17.33.0", {"start": v(516, 9.6) * mm, "mid": v(515.71, 10) * mm, "end": v(515.25, 10.16) * mm});
            skLineSegment(sketch, "E16.21.33.0", {"start": v(516, 9.6) * mm, "end": v(517.86, 3.7) * mm});
            skArc(sketch, "E16.24.33.0", {"start": v(518.16, 1.79) * mm, "mid": v(518.09, 2.76) * mm, "end": v(517.86, 3.7) * mm});
            skLineSegment(sketch, "E16.28.33.0", {"start": v(518.16, 1.79) * mm, "end": v(518.16, 0) * mm});
            skLineSegment(sketch, "E16.0.34.0", {"start": v(525.78, 0) * mm, "end": v(525.78, 1.79) * mm});
            skArc(sketch, "E16.3.34.0", {"start": v(526.08, 3.7) * mm, "mid": v(525.85, 2.76) * mm, "end": v(525.78, 1.79) * mm});
            skLineSegment(sketch, "E16.7.34.0", {"start": v(527.94, 9.6) * mm, "end": v(526.08, 3.7) * mm});
            skArc(sketch, "E16.10.34.0", {"start": v(528.7, 10.16) * mm, "mid": v(528.23, 10) * mm, "end": v(527.94, 9.6) * mm});
            skLineSegment(sketch, "E16.14.34.0", {"start": v(528.7, 10.16) * mm, "end": v(530.49, 10.16) * mm});
            skArc(sketch, "E16.17.34.0", {"start": v(531.24, 9.6) * mm, "mid": v(530.95, 10) * mm, "end": v(530.49, 10.16) * mm});
            skLineSegment(sketch, "E16.21.34.0", {"start": v(531.24, 9.6) * mm, "end": v(533.1, 3.7) * mm});
            skArc(sketch, "E16.24.34.0", {"start": v(533.4, 1.79) * mm, "mid": v(533.33, 2.76) * mm, "end": v(533.1, 3.7) * mm});
            skLineSegment(sketch, "E16.28.34.0", {"start": v(533.4, 1.79) * mm, "end": v(533.4, 0) * mm});
            skLineSegment(sketch, "E16.0.35.0", {"start": v(541.02, 0) * mm, "end": v(541.02, 1.79) * mm});
            skArc(sketch, "E16.3.35.0", {"start": v(541.32, 3.7) * mm, "mid": v(541.1, 2.76) * mm, "end": v(541.02, 1.79) * mm});
            skLineSegment(sketch, "E16.7.35.0", {"start": v(543.18, 9.6) * mm, "end": v(541.32, 3.7) * mm});
            skArc(sketch, "E16.10.35.0", {"start": v(543.93, 10.16) * mm, "mid": v(543.47, 10) * mm, "end": v(543.18, 9.6) * mm});
            skLineSegment(sketch, "E16.14.35.0", {"start": v(543.93, 10.16) * mm, "end": v(545.73, 10.16) * mm});
            skArc(sketch, "E16.17.35.0", {"start": v(546.48, 9.6) * mm, "mid": v(546.2, 10) * mm, "end": v(545.73, 10.16) * mm});
            skLineSegment(sketch, "E16.21.35.0", {"start": v(546.48, 9.6) * mm, "end": v(548.34, 3.7) * mm});
            skArc(sketch, "E16.24.35.0", {"start": v(548.64, 1.79) * mm, "mid": v(548.57, 2.76) * mm, "end": v(548.34, 3.7) * mm});
            skLineSegment(sketch, "E16.28.35.0", {"start": v(548.64, 1.79) * mm, "end": v(548.64, 0) * mm});
            skLineSegment(sketch, "E16.0.36.0", {"start": v(556.26, 0) * mm, "end": v(556.26, 1.79) * mm});
            skArc(sketch, "E16.3.36.0", {"start": v(556.56, 3.7) * mm, "mid": v(556.33, 2.76) * mm, "end": v(556.26, 1.79) * mm});
            skLineSegment(sketch, "E16.7.36.0", {"start": v(558.42, 9.6) * mm, "end": v(556.56, 3.7) * mm});
            skArc(sketch, "E16.10.36.0", {"start": v(559.17, 10.16) * mm, "mid": v(558.7, 10) * mm, "end": v(558.42, 9.6) * mm});
            skLineSegment(sketch, "E16.14.36.0", {"start": v(559.17, 10.16) * mm, "end": v(560.97, 10.16) * mm});
            skArc(sketch, "E16.17.36.0", {"start": v(561.72, 9.6) * mm, "mid": v(561.43, 10) * mm, "end": v(560.97, 10.16) * mm});
            skLineSegment(sketch, "E16.21.36.0", {"start": v(561.72, 9.6) * mm, "end": v(563.58, 3.7) * mm});
            skArc(sketch, "E16.24.36.0", {"start": v(563.88, 1.79) * mm, "mid": v(563.8, 2.76) * mm, "end": v(563.58, 3.7) * mm});
            skLineSegment(sketch, "E16.28.36.0", {"start": v(563.88, 1.79) * mm, "end": v(563.88, 0) * mm});
            skLineSegment(sketch, "E16.0.37.0", {"start": v(571.5, 0) * mm, "end": v(571.5, 1.79) * mm});
            skArc(sketch, "E16.3.37.0", {"start": v(571.8, 3.7) * mm, "mid": v(571.57, 2.76) * mm, "end": v(571.5, 1.79) * mm});
            skLineSegment(sketch, "E16.7.37.0", {"start": v(573.66, 9.6) * mm, "end": v(571.8, 3.7) * mm});
            skArc(sketch, "E16.10.37.0", {"start": v(574.41, 10.16) * mm, "mid": v(573.95, 10) * mm, "end": v(573.66, 9.6) * mm});
            skLineSegment(sketch, "E16.14.37.0", {"start": v(574.41, 10.16) * mm, "end": v(576.2, 10.16) * mm});
            skArc(sketch, "E16.17.37.0", {"start": v(576.96, 9.6) * mm, "mid": v(576.67, 10) * mm, "end": v(576.2, 10.16) * mm});
            skLineSegment(sketch, "E16.21.37.0", {"start": v(576.96, 9.6) * mm, "end": v(578.82, 3.7) * mm});
            skArc(sketch, "E16.24.37.0", {"start": v(579.12, 1.79) * mm, "mid": v(579.05, 2.76) * mm, "end": v(578.82, 3.7) * mm});
            skLineSegment(sketch, "E16.28.37.0", {"start": v(579.12, 1.79) * mm, "end": v(579.12, 0) * mm});
            skLineSegment(sketch, "E16.0.38.0", {"start": v(586.74, 0) * mm, "end": v(586.74, 1.79) * mm});
            skArc(sketch, "E16.3.38.0", {"start": v(587.04, 3.7) * mm, "mid": v(586.81, 2.76) * mm, "end": v(586.74, 1.79) * mm});
            skLineSegment(sketch, "E16.7.38.0", {"start": v(588.9, 9.6) * mm, "end": v(587.04, 3.7) * mm});
            skArc(sketch, "E16.10.38.0", {"start": v(589.65, 10.16) * mm, "mid": v(589.19, 10) * mm, "end": v(588.9, 9.6) * mm});
            skLineSegment(sketch, "E16.14.38.0", {"start": v(589.65, 10.16) * mm, "end": v(591.45, 10.16) * mm});
            skArc(sketch, "E16.17.38.0", {"start": v(592.2, 9.6) * mm, "mid": v(591.91, 10) * mm, "end": v(591.45, 10.16) * mm});
            skLineSegment(sketch, "E16.21.38.0", {"start": v(592.2, 9.6) * mm, "end": v(594.06, 3.7) * mm});
            skArc(sketch, "E16.24.38.0", {"start": v(594.36, 1.79) * mm, "mid": v(594.29, 2.76) * mm, "end": v(594.06, 3.7) * mm});
            skLineSegment(sketch, "E16.28.38.0", {"start": v(594.36, 1.79) * mm, "end": v(594.36, 0) * mm});
            skLineSegment(sketch, "E16.0.39.0", {"start": v(601.98, 0) * mm, "end": v(601.98, 1.79) * mm});
            skArc(sketch, "E16.3.39.0", {"start": v(602.28, 3.7) * mm, "mid": v(602.05, 2.76) * mm, "end": v(601.98, 1.79) * mm});
            skLineSegment(sketch, "E16.7.39.0", {"start": v(604.14, 9.6) * mm, "end": v(602.28, 3.7) * mm});
            skArc(sketch, "E16.10.39.0", {"start": v(604.9, 10.16) * mm, "mid": v(604.43, 10) * mm, "end": v(604.14, 9.6) * mm});
            skLineSegment(sketch, "E16.14.39.0", {"start": v(604.9, 10.16) * mm, "end": v(606.69, 10.16) * mm});
            skArc(sketch, "E16.17.39.0", {"start": v(607.44, 9.6) * mm, "mid": v(607.15, 10) * mm, "end": v(606.69, 10.16) * mm});
            skLineSegment(sketch, "E16.21.39.0", {"start": v(607.44, 9.6) * mm, "end": v(609.3, 3.7) * mm});
            skArc(sketch, "E16.24.39.0", {"start": v(609.6, 1.79) * mm, "mid": v(609.53, 2.76) * mm, "end": v(609.3, 3.7) * mm});
            skLineSegment(sketch, "E16.28.39.0", {"start": v(609.6, 1.79) * mm, "end": v(609.6, 0) * mm});
            skLineSegment(sketch, "E16.0.40.0", {"start": v(617.22, 0) * mm, "end": v(617.22, 1.79) * mm});
            skArc(sketch, "E16.3.40.0", {"start": v(617.52, 3.7) * mm, "mid": v(617.3, 2.76) * mm, "end": v(617.22, 1.79) * mm});
            skLineSegment(sketch, "E16.7.40.0", {"start": v(619.38, 9.6) * mm, "end": v(617.52, 3.7) * mm});
            skArc(sketch, "E16.10.40.0", {"start": v(620.13, 10.16) * mm, "mid": v(619.67, 10) * mm, "end": v(619.38, 9.6) * mm});
            skLineSegment(sketch, "E16.14.40.0", {"start": v(620.13, 10.16) * mm, "end": v(621.93, 10.16) * mm});
            skArc(sketch, "E16.17.40.0", {"start": v(622.68, 9.6) * mm, "mid": v(622.4, 10) * mm, "end": v(621.93, 10.16) * mm});
            skLineSegment(sketch, "E16.21.40.0", {"start": v(622.68, 9.6) * mm, "end": v(624.54, 3.7) * mm});
            skArc(sketch, "E16.24.40.0", {"start": v(624.84, 1.79) * mm, "mid": v(624.77, 2.76) * mm, "end": v(624.54, 3.7) * mm});
            skLineSegment(sketch, "E16.28.40.0", {"start": v(624.84, 1.79) * mm, "end": v(624.84, 0) * mm});
            skLineSegment(sketch, "E16.0.41.0", {"start": v(632.46, 0) * mm, "end": v(632.46, 1.79) * mm});
            skArc(sketch, "E16.3.41.0", {"start": v(632.76, 3.7) * mm, "mid": v(632.53, 2.76) * mm, "end": v(632.46, 1.79) * mm});
            skLineSegment(sketch, "E16.7.41.0", {"start": v(634.62, 9.6) * mm, "end": v(632.76, 3.7) * mm});
            skArc(sketch, "E16.10.41.0", {"start": v(635.37, 10.16) * mm, "mid": v(634.9, 10) * mm, "end": v(634.62, 9.6) * mm});
            skLineSegment(sketch, "E16.14.41.0", {"start": v(635.37, 10.16) * mm, "end": v(637.17, 10.16) * mm});
            skArc(sketch, "E16.17.41.0", {"start": v(637.92, 9.6) * mm, "mid": v(637.63, 10) * mm, "end": v(637.17, 10.16) * mm});
            skLineSegment(sketch, "E16.21.41.0", {"start": v(637.92, 9.6) * mm, "end": v(639.78, 3.7) * mm});
            skArc(sketch, "E16.24.41.0", {"start": v(640.08, 1.79) * mm, "mid": v(640, 2.76) * mm, "end": v(639.78, 3.7) * mm});
            skLineSegment(sketch, "E16.28.41.0", {"start": v(640.08, 1.79) * mm, "end": v(640.08, 0) * mm});
            skLineSegment(sketch, "E16.0.42.0", {"start": v(647.7, 0) * mm, "end": v(647.7, 1.79) * mm});
            skArc(sketch, "E16.3.42.0", {"start": v(648, 3.7) * mm, "mid": v(647.77, 2.76) * mm, "end": v(647.7, 1.79) * mm});
            skLineSegment(sketch, "E16.7.42.0", {"start": v(649.86, 9.6) * mm, "end": v(648, 3.7) * mm});
            skArc(sketch, "E16.10.42.0", {"start": v(650.61, 10.16) * mm, "mid": v(650.15, 10) * mm, "end": v(649.86, 9.6) * mm});
            skLineSegment(sketch, "E16.14.42.0", {"start": v(650.61, 10.16) * mm, "end": v(652.4, 10.16) * mm});
            skArc(sketch, "E16.17.42.0", {"start": v(653.16, 9.6) * mm, "mid": v(652.87, 10) * mm, "end": v(652.4, 10.16) * mm});
            skLineSegment(sketch, "E16.21.42.0", {"start": v(653.16, 9.6) * mm, "end": v(655.02, 3.7) * mm});
            skArc(sketch, "E16.24.42.0", {"start": v(655.32, 1.79) * mm, "mid": v(655.25, 2.76) * mm, "end": v(655.02, 3.7) * mm});
            skLineSegment(sketch, "E16.28.42.0", {"start": v(655.32, 1.79) * mm, "end": v(655.32, 0) * mm});
            skLineSegment(sketch, "E16.0.43.0", {"start": v(662.94, 0) * mm, "end": v(662.94, 1.79) * mm});
            skArc(sketch, "E16.3.43.0", {"start": v(663.24, 3.7) * mm, "mid": v(663.01, 2.76) * mm, "end": v(662.94, 1.79) * mm});
            skLineSegment(sketch, "E16.7.43.0", {"start": v(665.1, 9.6) * mm, "end": v(663.24, 3.7) * mm});
            skArc(sketch, "E16.10.43.0", {"start": v(665.85, 10.16) * mm, "mid": v(665.39, 10) * mm, "end": v(665.1, 9.6) * mm});
            skLineSegment(sketch, "E16.14.43.0", {"start": v(665.85, 10.16) * mm, "end": v(667.65, 10.16) * mm});
            skArc(sketch, "E16.17.43.0", {"start": v(668.4, 9.6) * mm, "mid": v(668.11, 10) * mm, "end": v(667.65, 10.16) * mm});
            skLineSegment(sketch, "E16.21.43.0", {"start": v(668.4, 9.6) * mm, "end": v(670.26, 3.7) * mm});
            skArc(sketch, "E16.24.43.0", {"start": v(670.56, 1.79) * mm, "mid": v(670.49, 2.76) * mm, "end": v(670.26, 3.7) * mm});
            skLineSegment(sketch, "E16.28.43.0", {"start": v(670.56, 1.79) * mm, "end": v(670.56, 0) * mm});
            skLineSegment(sketch, "E16.0.44.0", {"start": v(678.18, 0) * mm, "end": v(678.18, 1.79) * mm});
            skArc(sketch, "E16.3.44.0", {"start": v(678.48, 3.7) * mm, "mid": v(678.25, 2.76) * mm, "end": v(678.18, 1.79) * mm});
            skLineSegment(sketch, "E16.7.44.0", {"start": v(680.34, 9.6) * mm, "end": v(678.48, 3.7) * mm});
            skArc(sketch, "E16.10.44.0", {"start": v(681.1, 10.16) * mm, "mid": v(680.63, 10) * mm, "end": v(680.34, 9.6) * mm});
            skLineSegment(sketch, "E16.14.44.0", {"start": v(681.1, 10.16) * mm, "end": v(682.89, 10.16) * mm});
            skArc(sketch, "E16.17.44.0", {"start": v(683.64, 9.6) * mm, "mid": v(683.35, 10) * mm, "end": v(682.89, 10.16) * mm});
            skLineSegment(sketch, "E16.21.44.0", {"start": v(683.64, 9.6) * mm, "end": v(685.5, 3.7) * mm});
            skArc(sketch, "E16.24.44.0", {"start": v(685.8, 1.79) * mm, "mid": v(685.73, 2.76) * mm, "end": v(685.5, 3.7) * mm});
            skLineSegment(sketch, "E16.28.44.0", {"start": v(685.8, 1.79) * mm, "end": v(685.8, 0) * mm});
            skLineSegment(sketch, "E16.0.45.0", {"start": v(693.42, 0) * mm, "end": v(693.42, 1.79) * mm});
            skArc(sketch, "E16.3.45.0", {"start": v(693.72, 3.7) * mm, "mid": v(693.5, 2.76) * mm, "end": v(693.42, 1.79) * mm});
            skLineSegment(sketch, "E16.7.45.0", {"start": v(695.58, 9.6) * mm, "end": v(693.72, 3.7) * mm});
            skArc(sketch, "E16.10.45.0", {"start": v(696.33, 10.16) * mm, "mid": v(695.87, 10) * mm, "end": v(695.58, 9.6) * mm});
            skLineSegment(sketch, "E16.14.45.0", {"start": v(696.33, 10.16) * mm, "end": v(698.13, 10.16) * mm});
            skArc(sketch, "E16.17.45.0", {"start": v(698.88, 9.6) * mm, "mid": v(698.6, 10) * mm, "end": v(698.13, 10.16) * mm});
            skLineSegment(sketch, "E16.21.45.0", {"start": v(698.88, 9.6) * mm, "end": v(700.74, 3.7) * mm});
            skArc(sketch, "E16.24.45.0", {"start": v(701.04, 1.79) * mm, "mid": v(700.97, 2.76) * mm, "end": v(700.74, 3.7) * mm});
            skLineSegment(sketch, "E16.28.45.0", {"start": v(701.04, 1.79) * mm, "end": v(701.04, 0) * mm});
            skLineSegment(sketch, "E16.0.46.0", {"start": v(708.66, 0) * mm, "end": v(708.66, 1.79) * mm});
            skArc(sketch, "E16.3.46.0", {"start": v(708.96, 3.7) * mm, "mid": v(708.73, 2.76) * mm, "end": v(708.66, 1.79) * mm});
            skLineSegment(sketch, "E16.7.46.0", {"start": v(710.82, 9.6) * mm, "end": v(708.96, 3.7) * mm});
            skArc(sketch, "E16.10.46.0", {"start": v(711.57, 10.16) * mm, "mid": v(711.1, 10) * mm, "end": v(710.82, 9.6) * mm});
            skLineSegment(sketch, "E16.14.46.0", {"start": v(711.57, 10.16) * mm, "end": v(713.37, 10.16) * mm});
            skArc(sketch, "E16.17.46.0", {"start": v(714.12, 9.6) * mm, "mid": v(713.83, 10) * mm, "end": v(713.37, 10.16) * mm});
            skLineSegment(sketch, "E16.21.46.0", {"start": v(714.12, 9.6) * mm, "end": v(715.98, 3.7) * mm});
            skArc(sketch, "E16.24.46.0", {"start": v(716.28, 1.79) * mm, "mid": v(716.2, 2.76) * mm, "end": v(715.98, 3.7) * mm});
            skLineSegment(sketch, "E16.28.46.0", {"start": v(716.28, 1.79) * mm, "end": v(716.28, 0) * mm});
            skLineSegment(sketch, "E16.0.47.0", {"start": v(723.9, 0) * mm, "end": v(723.9, 1.79) * mm});
            skArc(sketch, "E16.3.47.0", {"start": v(724.2, 3.7) * mm, "mid": v(723.97, 2.76) * mm, "end": v(723.9, 1.79) * mm});
            skLineSegment(sketch, "E16.7.47.0", {"start": v(726.06, 9.6) * mm, "end": v(724.2, 3.7) * mm});
            skArc(sketch, "E16.10.47.0", {"start": v(726.81, 10.16) * mm, "mid": v(726.35, 10) * mm, "end": v(726.06, 9.6) * mm});
            skLineSegment(sketch, "E16.14.47.0", {"start": v(726.81, 10.16) * mm, "end": v(728.6, 10.16) * mm});
            skArc(sketch, "E16.17.47.0", {"start": v(729.36, 9.6) * mm, "mid": v(729.07, 10) * mm, "end": v(728.6, 10.16) * mm});
            skLineSegment(sketch, "E16.21.47.0", {"start": v(729.36, 9.6) * mm, "end": v(731.22, 3.7) * mm});
            skArc(sketch, "E16.24.47.0", {"start": v(731.52, 1.79) * mm, "mid": v(731.45, 2.76) * mm, "end": v(731.22, 3.7) * mm});
            skLineSegment(sketch, "E16.28.47.0", {"start": v(731.52, 1.79) * mm, "end": v(731.52, 0) * mm});
            skLineSegment(sketch, "E16.0.48.0", {"start": v(739.14, 0) * mm, "end": v(739.14, 1.79) * mm});
            skArc(sketch, "E16.3.48.0", {"start": v(739.44, 3.7) * mm, "mid": v(739.21, 2.76) * mm, "end": v(739.14, 1.79) * mm});
            skLineSegment(sketch, "E16.7.48.0", {"start": v(741.3, 9.6) * mm, "end": v(739.44, 3.7) * mm});
            skArc(sketch, "E16.10.48.0", {"start": v(742.05, 10.16) * mm, "mid": v(741.59, 10) * mm, "end": v(741.3, 9.6) * mm});
            skLineSegment(sketch, "E16.14.48.0", {"start": v(742.05, 10.16) * mm, "end": v(743.85, 10.16) * mm});
            skArc(sketch, "E16.17.48.0", {"start": v(744.6, 9.6) * mm, "mid": v(744.31, 10) * mm, "end": v(743.85, 10.16) * mm});
            skLineSegment(sketch, "E16.21.48.0", {"start": v(744.6, 9.6) * mm, "end": v(746.46, 3.7) * mm});
            skArc(sketch, "E16.24.48.0", {"start": v(746.76, 1.79) * mm, "mid": v(746.69, 2.76) * mm, "end": v(746.46, 3.7) * mm});
            skLineSegment(sketch, "E16.28.48.0", {"start": v(746.76, 1.79) * mm, "end": v(746.76, 0) * mm});
            skLineSegment(sketch, "E16.0.49.0", {"start": v(754.38, 0) * mm, "end": v(754.38, 1.79) * mm});
            skArc(sketch, "E16.3.49.0", {"start": v(754.68, 3.7) * mm, "mid": v(754.45, 2.76) * mm, "end": v(754.38, 1.79) * mm});
            skLineSegment(sketch, "E16.7.49.0", {"start": v(756.54, 9.6) * mm, "end": v(754.68, 3.7) * mm});
            skArc(sketch, "E16.10.49.0", {"start": v(757.3, 10.16) * mm, "mid": v(756.83, 10) * mm, "end": v(756.54, 9.6) * mm});
            skLineSegment(sketch, "E16.14.49.0", {"start": v(757.3, 10.16) * mm, "end": v(759.09, 10.16) * mm});
            skArc(sketch, "E16.17.49.0", {"start": v(759.84, 9.6) * mm, "mid": v(759.55, 10) * mm, "end": v(759.09, 10.16) * mm});
            skLineSegment(sketch, "E16.21.49.0", {"start": v(759.84, 9.6) * mm, "end": v(761.7, 3.7) * mm});
            skArc(sketch, "E16.24.49.0", {"start": v(762, 1.79) * mm, "mid": v(761.93, 2.76) * mm, "end": v(761.7, 3.7) * mm});
            skLineSegment(sketch, "E16.28.49.0", {"start": v(762, 1.79) * mm, "end": v(762, 0) * mm});
            skSolve(sketch);
        }
        {
            var Q0;
            Q0 = qSketchRegion(id + "F0", true);
            extrude(context, id + "F1", {"entities" : qUnion([Q0]), "depth" : 127 * mm});
        }
        {
            var Q0;
            Q0=makeQuery(id+"F0.imprint","IMPRINT",FACE,{"disambiguationData":[TD([[makeQuery(id+"F0.imprint","IMPRINT",EDGE,{"derivedFrom":sQuery(id+"F0.wireOp",EDGE,"E0")}),1.0]])]});
            var sketch = newSketch(context, id + "F2", { "sketchPlane" : qUnion([Q0])});
            skLineSegment(sketch, "E17", {"start": v(0, 0) * mm, "end": v(0, -6.35) * mm});
            skLineSegment(sketch, "E18", {"start": v(0, -6.35) * mm, "end": v(50.8, -6.35) * mm});
            skLineSegment(sketch, "E19.0", {"start": v(0, -19.05) * mm, "end": v(762, -19.05) * mm});
            skLineSegment(sketch, "E20", {"start": v(50.8, -6.35) * mm, "end": v(50.8, -19.05) * mm});
            skLineSegment(sketch, "E21", {"start": v(762, -19.05) * mm, "end": v(762, -6.35) * mm});
            skLineSegment(sketch, "E22", {"start": v(762, -6.35) * mm, "end": v(711.2, -6.35) * mm});
            skLineSegment(sketch, "E23", {"start": v(711.2, -6.35) * mm, "end": v(711.2, -19.05) * mm});
            skLineSegment(sketch, "E24", {"start": v(0, -19.05) * mm, "end": v(0, -6.35) * mm});
            skLineSegment(sketch, "E25", {"start": v(50.8, -19.05) * mm, "end": v(50.8, -6.35) * mm});
            skSolve(sketch);
        }
        {
            var Q0;
            Q0=makeQuery(id+"F2.imprint","IMPRINT",FACE,{"disambiguationData":[TD([[makeQuery(id+"F2.imprint","IMPRINT",EDGE,{"derivedFrom":sQuery(id+"F2.wireOp",EDGE,"E18")}),-1.0]])]});
            var Q1;
            {var subQ0=sQuery(id+"F2.wireOp",EDGE,"E21");Q1=makeQuery(id+"F2.imprint","IMPRINT",FACE,{"disambiguationData":[TD([[makeQuery(id+"F2.imprint","IMPRINT",EDGE,{"derivedFrom":subQ0}),1.0]])]});}
            extrude(context, id + "F3", {"entities" : qUnion([Q0, Q1]), "operationType" : NewBodyOperationType.ADD, "oppositeDirection" : true, "depth" : 25.4 * mm});
        }
        {
            var Q0;
            Q0=makeQuery(id+"F1.opExtrude","CAP_FACE",FACE,{"disambiguationData":[OSD([sQuery(id+"F0.wireOp",EDGE,"E0"),sQuery(id+"F0.wireOp",EDGE,"E1"),sQuery(id+"F0.wireOp",EDGE,"E2"),sQuery(id+"F0.wireOp",EDGE,"E3"),sQuery(id+"F0.wireOp",EDGE,"E4"),sQuery(id+"F0.wireOp",EDGE,"E5"),sQuery(id+"F0.wireOp",EDGE,"E6"),sQuery(id+"F0.wireOp",EDGE,"E7"),sQuery(id+"F0.wireOp",EDGE,"E8"),sQuery(id+"F0.wireOp",EDGE,"E9"),sQuery(id+"F0.wireOp",EDGE,"E10.filletArc"),sQuery(id+"F0.wireOp",EDGE,"E11.filletArc"),sQuery(id+"F0.wireOp",EDGE,"E12.filletArc"),sQuery(id+"F0.wireOp",EDGE,"E13.filletArc"),sQuery(id+"F0.wireOp",EDGE,"E14"),sQuery(id+"F0.wireOp",EDGE,"E15.1.0.0"),sQuery(id+"F0.wireOp",EDGE,"E15.1.0.1"),sQuery(id+"F0.wireOp",EDGE,"E15.1.0.2"),sQuery(id+"F0.wireOp",EDGE,"E15.1.0.3"),sQuery(id+"F0.wireOp",EDGE,"E15.1.0.4"),sQuery(id+"F0.wireOp",EDGE,"E15.1.0.5"),sQuery(id+"F0.wireOp",EDGE,"E15.1.0.6"),sQuery(id+"F0.wireOp",EDGE,"E15.1.0.7"),sQuery(id+"F0.wireOp",EDGE,"E15.1.0.8"),sQuery(id+"F0.wireOp",EDGE,"E15.2.0.0"),sQuery(id+"F0.wireOp",EDGE,"E15.2.0.1"),sQuery(id+"F0.wireOp",EDGE,"E15.2.0.2"),sQuery(id+"F0.wireOp",EDGE,"E15.2.0.3"),sQuery(id+"F0.wireOp",EDGE,"E15.2.0.4"),sQuery(id+"F0.wireOp",EDGE,"E15.2.0.5"),sQuery(id+"F0.wireOp",EDGE,"E15.2.0.6"),sQuery(id+"F0.wireOp",EDGE,"E15.2.0.7"),sQuery(id+"F0.wireOp",EDGE,"E15.2.0.8"),sQuery(id+"F0.wireOp",EDGE,"E16.0.3.0"),sQuery(id+"F0.wireOp",EDGE,"E16.3.3.0"),sQuery(id+"F0.wireOp",EDGE,"E16.7.3.0"),sQuery(id+"F0.wireOp",EDGE,"E16.10.3.0"),sQuery(id+"F0.wireOp",EDGE,"E16.14.3.0"),sQuery(id+"F0.wireOp",EDGE,"E16.17.3.0"),sQuery(id+"F0.wireOp",EDGE,"E16.21.3.0"),sQuery(id+"F0.wireOp",EDGE,"E16.24.3.0"),sQuery(id+"F0.wireOp",EDGE,"E16.28.3.0"),sQuery(id+"F0.wireOp",EDGE,"E16.0.4.0"),sQuery(id+"F0.wireOp",EDGE,"E16.3.4.0"),sQuery(id+"F0.wireOp",EDGE,"E16.7.4.0"),sQuery(id+"F0.wireOp",EDGE,"E16.10.4.0"),sQuery(id+"F0.wireOp",EDGE,"E16.14.4.0"),sQuery(id+"F0.wireOp",EDGE,"E16.17.4.0"),sQuery(id+"F0.wireOp",EDGE,"E16.21.4.0"),sQuery(id+"F0.wireOp",EDGE,"E16.24.4.0"),sQuery(id+"F0.wireOp",EDGE,"E16.28.4.0"),sQuery(id+"F0.wireOp",EDGE,"E16.0.5.0"),sQuery(id+"F0.wireOp",EDGE,"E16.3.5.0"),sQuery(id+"F0.wireOp",EDGE,"E16.7.5.0"),sQuery(id+"F0.wireOp",EDGE,"E16.10.5.0"),sQuery(id+"F0.wireOp",EDGE,"E16.14.5.0"),sQuery(id+"F0.wireOp",EDGE,"E16.17.5.0"),sQuery(id+"F0.wireOp",EDGE,"E16.21.5.0"),sQuery(id+"F0.wireOp",EDGE,"E16.24.5.0"),sQuery(id+"F0.wireOp",EDGE,"E16.28.5.0"),sQuery(id+"F0.wireOp",EDGE,"E16.0.6.0"),sQuery(id+"F0.wireOp",EDGE,"E16.3.6.0"),sQuery(id+"F0.wireOp",EDGE,"E16.7.6.0"),sQuery(id+"F0.wireOp",EDGE,"E16.10.6.0"),sQuery(id+"F0.wireOp",EDGE,"E16.14.6.0"),sQuery(id+"F0.wireOp",EDGE,"E16.17.6.0"),sQuery(id+"F0.wireOp",EDGE,"E16.21.6.0"),sQuery(id+"F0.wireOp",EDGE,"E16.24.6.0"),sQuery(id+"F0.wireOp",EDGE,"E16.28.6.0"),sQuery(id+"F0.wireOp",EDGE,"E16.0.7.0"),sQuery(id+"F0.wireOp",EDGE,"E16.3.7.0"),sQuery(id+"F0.wireOp",EDGE,"E16.7.7.0"),sQuery(id+"F0.wireOp",EDGE,"E16.10.7.0"),sQuery(id+"F0.wireOp",EDGE,"E16.14.7.0"),sQuery(id+"F0.wireOp",EDGE,"E16.17.7.0"),sQuery(id+"F0.wireOp",EDGE,"E16.21.7.0"),sQuery(id+"F0.wireOp",EDGE,"E16.24.7.0"),sQuery(id+"F0.wireOp",EDGE,"E16.28.7.0"),sQuery(id+"F0.wireOp",EDGE,"E16.0.8.0"),sQuery(id+"F0.wireOp",EDGE,"E16.3.8.0"),sQuery(id+"F0.wireOp",EDGE,"E16.7.8.0"),sQuery(id+"F0.wireOp",EDGE,"E16.10.8.0"),sQuery(id+"F0.wireOp",EDGE,"E16.14.8.0"),sQuery(id+"F0.wireOp",EDGE,"E16.17.8.0"),sQuery(id+"F0.wireOp",EDGE,"E16.21.8.0"),sQuery(id+"F0.wireOp",EDGE,"E16.24.8.0"),sQuery(id+"F0.wireOp",EDGE,"E16.28.8.0"),sQuery(id+"F0.wireOp",EDGE,"E16.0.9.0"),sQuery(id+"F0.wireOp",EDGE,"E16.3.9.0"),sQuery(id+"F0.wireOp",EDGE,"E16.7.9.0"),sQuery(id+"F0.wireOp",EDGE,"E16.10.9.0"),sQuery(id+"F0.wireOp",EDGE,"E16.14.9.0"),sQuery(id+"F0.wireOp",EDGE,"E16.17.9.0"),sQuery(id+"F0.wireOp",EDGE,"E16.21.9.0"),sQuery(id+"F0.wireOp",EDGE,"E16.24.9.0"),sQuery(id+"F0.wireOp",EDGE,"E16.28.9.0"),sQuery(id+"F0.wireOp",EDGE,"E16.0.10.0"),sQuery(id+"F0.wireOp",EDGE,"E16.3.10.0"),sQuery(id+"F0.wireOp",EDGE,"E16.7.10.0"),sQuery(id+"F0.wireOp",EDGE,"E16.10.10.0"),sQuery(id+"F0.wireOp",EDGE,"E16.14.10.0"),sQuery(id+"F0.wireOp",EDGE,"E16.17.10.0"),sQuery(id+"F0.wireOp",EDGE,"E16.21.10.0"),sQuery(id+"F0.wireOp",EDGE,"E16.24.10.0"),sQuery(id+"F0.wireOp",EDGE,"E16.28.10.0"),sQuery(id+"F0.wireOp",EDGE,"E16.0.11.0"),sQuery(id+"F0.wireOp",EDGE,"E16.3.11.0"),sQuery(id+"F0.wireOp",EDGE,"E16.7.11.0"),sQuery(id+"F0.wireOp",EDGE,"E16.10.11.0"),sQuery(id+"F0.wireOp",EDGE,"E16.14.11.0"),sQuery(id+"F0.wireOp",EDGE,"E16.17.11.0"),sQuery(id+"F0.wireOp",EDGE,"E16.21.11.0"),sQuery(id+"F0.wireOp",EDGE,"E16.24.11.0"),sQuery(id+"F0.wireOp",EDGE,"E16.28.11.0"),sQuery(id+"F0.wireOp",EDGE,"E16.0.12.0"),sQuery(id+"F0.wireOp",EDGE,"E16.3.12.0"),sQuery(id+"F0.wireOp",EDGE,"E16.7.12.0"),sQuery(id+"F0.wireOp",EDGE,"E16.10.12.0"),sQuery(id+"F0.wireOp",EDGE,"E16.14.12.0"),sQuery(id+"F0.wireOp",EDGE,"E16.17.12.0"),sQuery(id+"F0.wireOp",EDGE,"E16.21.12.0"),sQuery(id+"F0.wireOp",EDGE,"E16.24.12.0"),sQuery(id+"F0.wireOp",EDGE,"E16.28.12.0"),sQuery(id+"F0.wireOp",EDGE,"E16.0.13.0"),sQuery(id+"F0.wireOp",EDGE,"E16.3.13.0"),sQuery(id+"F0.wireOp",EDGE,"E16.7.13.0"),sQuery(id+"F0.wireOp",EDGE,"E16.10.13.0"),sQuery(id+"F0.wireOp",EDGE,"E16.14.13.0"),sQuery(id+"F0.wireOp",EDGE,"E16.17.13.0"),sQuery(id+"F0.wireOp",EDGE,"E16.21.13.0"),sQuery(id+"F0.wireOp",EDGE,"E16.24.13.0"),sQuery(id+"F0.wireOp",EDGE,"E16.28.13.0"),sQuery(id+"F0.wireOp",EDGE,"E16.0.14.0"),sQuery(id+"F0.wireOp",EDGE,"E16.3.14.0"),sQuery(id+"F0.wireOp",EDGE,"E16.7.14.0"),sQuery(id+"F0.wireOp",EDGE,"E16.10.14.0"),sQuery(id+"F0.wireOp",EDGE,"E16.14.14.0"),sQuery(id+"F0.wireOp",EDGE,"E16.17.14.0"),sQuery(id+"F0.wireOp",EDGE,"E16.21.14.0"),sQuery(id+"F0.wireOp",EDGE,"E16.24.14.0"),sQuery(id+"F0.wireOp",EDGE,"E16.28.14.0"),sQuery(id+"F0.wireOp",EDGE,"E16.0.15.0"),sQuery(id+"F0.wireOp",EDGE,"E16.3.15.0"),sQuery(id+"F0.wireOp",EDGE,"E16.7.15.0"),sQuery(id+"F0.wireOp",EDGE,"E16.10.15.0"),sQuery(id+"F0.wireOp",EDGE,"E16.14.15.0"),sQuery(id+"F0.wireOp",EDGE,"E16.17.15.0"),sQuery(id+"F0.wireOp",EDGE,"E16.21.15.0"),sQuery(id+"F0.wireOp",EDGE,"E16.24.15.0"),sQuery(id+"F0.wireOp",EDGE,"E16.28.15.0"),sQuery(id+"F0.wireOp",EDGE,"E16.0.16.0"),sQuery(id+"F0.wireOp",EDGE,"E16.3.16.0"),sQuery(id+"F0.wireOp",EDGE,"E16.7.16.0"),sQuery(id+"F0.wireOp",EDGE,"E16.10.16.0"),sQuery(id+"F0.wireOp",EDGE,"E16.14.16.0"),sQuery(id+"F0.wireOp",EDGE,"E16.17.16.0"),sQuery(id+"F0.wireOp",EDGE,"E16.21.16.0"),sQuery(id+"F0.wireOp",EDGE,"E16.24.16.0"),sQuery(id+"F0.wireOp",EDGE,"E16.28.16.0"),sQuery(id+"F0.wireOp",EDGE,"E16.0.17.0"),sQuery(id+"F0.wireOp",EDGE,"E16.3.17.0"),sQuery(id+"F0.wireOp",EDGE,"E16.7.17.0"),sQuery(id+"F0.wireOp",EDGE,"E16.10.17.0"),sQuery(id+"F0.wireOp",EDGE,"E16.14.17.0"),sQuery(id+"F0.wireOp",EDGE,"E16.17.17.0"),sQuery(id+"F0.wireOp",EDGE,"E16.21.17.0"),sQuery(id+"F0.wireOp",EDGE,"E16.24.17.0"),sQuery(id+"F0.wireOp",EDGE,"E16.28.17.0"),sQuery(id+"F0.wireOp",EDGE,"E16.0.18.0"),sQuery(id+"F0.wireOp",EDGE,"E16.3.18.0"),sQuery(id+"F0.wireOp",EDGE,"E16.7.18.0"),sQuery(id+"F0.wireOp",EDGE,"E16.10.18.0"),sQuery(id+"F0.wireOp",EDGE,"E16.14.18.0"),sQuery(id+"F0.wireOp",EDGE,"E16.17.18.0"),sQuery(id+"F0.wireOp",EDGE,"E16.21.18.0"),sQuery(id+"F0.wireOp",EDGE,"E16.24.18.0"),sQuery(id+"F0.wireOp",EDGE,"E16.28.18.0"),sQuery(id+"F0.wireOp",EDGE,"E16.0.19.0"),sQuery(id+"F0.wireOp",EDGE,"E16.3.19.0"),sQuery(id+"F0.wireOp",EDGE,"E16.7.19.0"),sQuery(id+"F0.wireOp",EDGE,"E16.10.19.0"),sQuery(id+"F0.wireOp",EDGE,"E16.14.19.0"),sQuery(id+"F0.wireOp",EDGE,"E16.17.19.0"),sQuery(id+"F0.wireOp",EDGE,"E16.21.19.0"),sQuery(id+"F0.wireOp",EDGE,"E16.24.19.0"),sQuery(id+"F0.wireOp",EDGE,"E16.28.19.0"),sQuery(id+"F0.wireOp",EDGE,"E16.0.20.0"),sQuery(id+"F0.wireOp",EDGE,"E16.3.20.0"),sQuery(id+"F0.wireOp",EDGE,"E16.7.20.0"),sQuery(id+"F0.wireOp",EDGE,"E16.10.20.0"),sQuery(id+"F0.wireOp",EDGE,"E16.14.20.0"),sQuery(id+"F0.wireOp",EDGE,"E16.17.20.0"),sQuery(id+"F0.wireOp",EDGE,"E16.21.20.0"),sQuery(id+"F0.wireOp",EDGE,"E16.24.20.0"),sQuery(id+"F0.wireOp",EDGE,"E16.28.20.0"),sQuery(id+"F0.wireOp",EDGE,"E16.0.21.0"),sQuery(id+"F0.wireOp",EDGE,"E16.3.21.0"),sQuery(id+"F0.wireOp",EDGE,"E16.7.21.0"),sQuery(id+"F0.wireOp",EDGE,"E16.10.21.0"),sQuery(id+"F0.wireOp",EDGE,"E16.14.21.0"),sQuery(id+"F0.wireOp",EDGE,"E16.17.21.0"),sQuery(id+"F0.wireOp",EDGE,"E16.21.21.0"),sQuery(id+"F0.wireOp",EDGE,"E16.24.21.0"),sQuery(id+"F0.wireOp",EDGE,"E16.28.21.0"),sQuery(id+"F0.wireOp",EDGE,"E16.0.22.0"),sQuery(id+"F0.wireOp",EDGE,"E16.3.22.0"),sQuery(id+"F0.wireOp",EDGE,"E16.7.22.0"),sQuery(id+"F0.wireOp",EDGE,"E16.10.22.0"),sQuery(id+"F0.wireOp",EDGE,"E16.14.22.0"),sQuery(id+"F0.wireOp",EDGE,"E16.17.22.0"),sQuery(id+"F0.wireOp",EDGE,"E16.21.22.0"),sQuery(id+"F0.wireOp",EDGE,"E16.24.22.0"),sQuery(id+"F0.wireOp",EDGE,"E16.28.22.0"),sQuery(id+"F0.wireOp",EDGE,"E16.0.23.0"),sQuery(id+"F0.wireOp",EDGE,"E16.3.23.0"),sQuery(id+"F0.wireOp",EDGE,"E16.7.23.0"),sQuery(id+"F0.wireOp",EDGE,"E16.10.23.0"),sQuery(id+"F0.wireOp",EDGE,"E16.14.23.0"),sQuery(id+"F0.wireOp",EDGE,"E16.17.23.0"),sQuery(id+"F0.wireOp",EDGE,"E16.21.23.0"),sQuery(id+"F0.wireOp",EDGE,"E16.24.23.0"),sQuery(id+"F0.wireOp",EDGE,"E16.28.23.0"),sQuery(id+"F0.wireOp",EDGE,"E16.0.24.0"),sQuery(id+"F0.wireOp",EDGE,"E16.3.24.0"),sQuery(id+"F0.wireOp",EDGE,"E16.7.24.0"),sQuery(id+"F0.wireOp",EDGE,"E16.10.24.0"),sQuery(id+"F0.wireOp",EDGE,"E16.14.24.0"),sQuery(id+"F0.wireOp",EDGE,"E16.17.24.0"),sQuery(id+"F0.wireOp",EDGE,"E16.21.24.0"),sQuery(id+"F0.wireOp",EDGE,"E16.24.24.0"),sQuery(id+"F0.wireOp",EDGE,"E16.28.24.0"),sQuery(id+"F0.wireOp",EDGE,"E16.0.25.0"),sQuery(id+"F0.wireOp",EDGE,"E16.3.25.0"),sQuery(id+"F0.wireOp",EDGE,"E16.7.25.0"),sQuery(id+"F0.wireOp",EDGE,"E16.10.25.0"),sQuery(id+"F0.wireOp",EDGE,"E16.14.25.0"),sQuery(id+"F0.wireOp",EDGE,"E16.17.25.0"),sQuery(id+"F0.wireOp",EDGE,"E16.21.25.0"),sQuery(id+"F0.wireOp",EDGE,"E16.24.25.0"),sQuery(id+"F0.wireOp",EDGE,"E16.28.25.0"),sQuery(id+"F0.wireOp",EDGE,"E16.0.26.0"),sQuery(id+"F0.wireOp",EDGE,"E16.3.26.0"),sQuery(id+"F0.wireOp",EDGE,"E16.7.26.0"),sQuery(id+"F0.wireOp",EDGE,"E16.10.26.0"),sQuery(id+"F0.wireOp",EDGE,"E16.14.26.0"),sQuery(id+"F0.wireOp",EDGE,"E16.17.26.0"),sQuery(id+"F0.wireOp",EDGE,"E16.21.26.0"),sQuery(id+"F0.wireOp",EDGE,"E16.24.26.0"),sQuery(id+"F0.wireOp",EDGE,"E16.28.26.0"),sQuery(id+"F0.wireOp",EDGE,"E16.0.27.0"),sQuery(id+"F0.wireOp",EDGE,"E16.3.27.0"),sQuery(id+"F0.wireOp",EDGE,"E16.7.27.0"),sQuery(id+"F0.wireOp",EDGE,"E16.10.27.0"),sQuery(id+"F0.wireOp",EDGE,"E16.14.27.0"),sQuery(id+"F0.wireOp",EDGE,"E16.17.27.0"),sQuery(id+"F0.wireOp",EDGE,"E16.21.27.0"),sQuery(id+"F0.wireOp",EDGE,"E16.24.27.0"),sQuery(id+"F0.wireOp",EDGE,"E16.28.27.0"),sQuery(id+"F0.wireOp",EDGE,"E16.0.28.0"),sQuery(id+"F0.wireOp",EDGE,"E16.3.28.0"),sQuery(id+"F0.wireOp",EDGE,"E16.7.28.0"),sQuery(id+"F0.wireOp",EDGE,"E16.10.28.0"),sQuery(id+"F0.wireOp",EDGE,"E16.14.28.0"),sQuery(id+"F0.wireOp",EDGE,"E16.17.28.0"),sQuery(id+"F0.wireOp",EDGE,"E16.21.28.0"),sQuery(id+"F0.wireOp",EDGE,"E16.24.28.0"),sQuery(id+"F0.wireOp",EDGE,"E16.28.28.0"),sQuery(id+"F0.wireOp",EDGE,"E16.0.29.0"),sQuery(id+"F0.wireOp",EDGE,"E16.3.29.0"),sQuery(id+"F0.wireOp",EDGE,"E16.7.29.0"),sQuery(id+"F0.wireOp",EDGE,"E16.10.29.0"),sQuery(id+"F0.wireOp",EDGE,"E16.14.29.0"),sQuery(id+"F0.wireOp",EDGE,"E16.17.29.0"),sQuery(id+"F0.wireOp",EDGE,"E16.21.29.0"),sQuery(id+"F0.wireOp",EDGE,"E16.24.29.0"),sQuery(id+"F0.wireOp",EDGE,"E16.28.29.0"),sQuery(id+"F0.wireOp",EDGE,"E16.0.30.0"),sQuery(id+"F0.wireOp",EDGE,"E16.3.30.0"),sQuery(id+"F0.wireOp",EDGE,"E16.7.30.0"),sQuery(id+"F0.wireOp",EDGE,"E16.10.30.0"),sQuery(id+"F0.wireOp",EDGE,"E16.14.30.0"),sQuery(id+"F0.wireOp",EDGE,"E16.17.30.0"),sQuery(id+"F0.wireOp",EDGE,"E16.21.30.0"),sQuery(id+"F0.wireOp",EDGE,"E16.24.30.0"),sQuery(id+"F0.wireOp",EDGE,"E16.28.30.0"),sQuery(id+"F0.wireOp",EDGE,"E16.0.31.0"),sQuery(id+"F0.wireOp",EDGE,"E16.3.31.0"),sQuery(id+"F0.wireOp",EDGE,"E16.7.31.0"),sQuery(id+"F0.wireOp",EDGE,"E16.10.31.0"),sQuery(id+"F0.wireOp",EDGE,"E16.14.31.0"),sQuery(id+"F0.wireOp",EDGE,"E16.17.31.0"),sQuery(id+"F0.wireOp",EDGE,"E16.21.31.0"),sQuery(id+"F0.wireOp",EDGE,"E16.24.31.0"),sQuery(id+"F0.wireOp",EDGE,"E16.28.31.0"),sQuery(id+"F0.wireOp",EDGE,"E16.0.32.0"),sQuery(id+"F0.wireOp",EDGE,"E16.3.32.0"),sQuery(id+"F0.wireOp",EDGE,"E16.7.32.0"),sQuery(id+"F0.wireOp",EDGE,"E16.10.32.0"),sQuery(id+"F0.wireOp",EDGE,"E16.14.32.0"),sQuery(id+"F0.wireOp",EDGE,"E16.17.32.0"),sQuery(id+"F0.wireOp",EDGE,"E16.21.32.0"),sQuery(id+"F0.wireOp",EDGE,"E16.24.32.0"),sQuery(id+"F0.wireOp",EDGE,"E16.28.32.0"),sQuery(id+"F0.wireOp",EDGE,"E16.0.33.0"),sQuery(id+"F0.wireOp",EDGE,"E16.3.33.0"),sQuery(id+"F0.wireOp",EDGE,"E16.7.33.0"),sQuery(id+"F0.wireOp",EDGE,"E16.10.33.0"),sQuery(id+"F0.wireOp",EDGE,"E16.14.33.0"),sQuery(id+"F0.wireOp",EDGE,"E16.17.33.0"),sQuery(id+"F0.wireOp",EDGE,"E16.21.33.0"),sQuery(id+"F0.wireOp",EDGE,"E16.24.33.0"),sQuery(id+"F0.wireOp",EDGE,"E16.28.33.0"),sQuery(id+"F0.wireOp",EDGE,"E16.0.34.0"),sQuery(id+"F0.wireOp",EDGE,"E16.3.34.0"),sQuery(id+"F0.wireOp",EDGE,"E16.7.34.0"),sQuery(id+"F0.wireOp",EDGE,"E16.10.34.0"),sQuery(id+"F0.wireOp",EDGE,"E16.14.34.0"),sQuery(id+"F0.wireOp",EDGE,"E16.17.34.0"),sQuery(id+"F0.wireOp",EDGE,"E16.21.34.0"),sQuery(id+"F0.wireOp",EDGE,"E16.24.34.0"),sQuery(id+"F0.wireOp",EDGE,"E16.28.34.0"),sQuery(id+"F0.wireOp",EDGE,"E16.0.35.0"),sQuery(id+"F0.wireOp",EDGE,"E16.3.35.0"),sQuery(id+"F0.wireOp",EDGE,"E16.7.35.0"),sQuery(id+"F0.wireOp",EDGE,"E16.10.35.0"),sQuery(id+"F0.wireOp",EDGE,"E16.14.35.0"),sQuery(id+"F0.wireOp",EDGE,"E16.17.35.0"),sQuery(id+"F0.wireOp",EDGE,"E16.21.35.0"),sQuery(id+"F0.wireOp",EDGE,"E16.24.35.0"),sQuery(id+"F0.wireOp",EDGE,"E16.28.35.0"),sQuery(id+"F0.wireOp",EDGE,"E16.0.36.0"),sQuery(id+"F0.wireOp",EDGE,"E16.3.36.0"),sQuery(id+"F0.wireOp",EDGE,"E16.7.36.0"),sQuery(id+"F0.wireOp",EDGE,"E16.10.36.0"),sQuery(id+"F0.wireOp",EDGE,"E16.14.36.0"),sQuery(id+"F0.wireOp",EDGE,"E16.17.36.0"),sQuery(id+"F0.wireOp",EDGE,"E16.21.36.0"),sQuery(id+"F0.wireOp",EDGE,"E16.24.36.0"),sQuery(id+"F0.wireOp",EDGE,"E16.28.36.0"),sQuery(id+"F0.wireOp",EDGE,"E16.0.37.0"),sQuery(id+"F0.wireOp",EDGE,"E16.3.37.0"),sQuery(id+"F0.wireOp",EDGE,"E16.7.37.0"),sQuery(id+"F0.wireOp",EDGE,"E16.10.37.0"),sQuery(id+"F0.wireOp",EDGE,"E16.14.37.0"),sQuery(id+"F0.wireOp",EDGE,"E16.17.37.0"),sQuery(id+"F0.wireOp",EDGE,"E16.21.37.0"),sQuery(id+"F0.wireOp",EDGE,"E16.24.37.0"),sQuery(id+"F0.wireOp",EDGE,"E16.28.37.0"),sQuery(id+"F0.wireOp",EDGE,"E16.0.38.0"),sQuery(id+"F0.wireOp",EDGE,"E16.3.38.0"),sQuery(id+"F0.wireOp",EDGE,"E16.7.38.0"),sQuery(id+"F0.wireOp",EDGE,"E16.10.38.0"),sQuery(id+"F0.wireOp",EDGE,"E16.14.38.0"),sQuery(id+"F0.wireOp",EDGE,"E16.17.38.0"),sQuery(id+"F0.wireOp",EDGE,"E16.21.38.0"),sQuery(id+"F0.wireOp",EDGE,"E16.24.38.0"),sQuery(id+"F0.wireOp",EDGE,"E16.28.38.0"),sQuery(id+"F0.wireOp",EDGE,"E16.0.39.0"),sQuery(id+"F0.wireOp",EDGE,"E16.3.39.0"),sQuery(id+"F0.wireOp",EDGE,"E16.7.39.0"),sQuery(id+"F0.wireOp",EDGE,"E16.10.39.0"),sQuery(id+"F0.wireOp",EDGE,"E16.14.39.0"),sQuery(id+"F0.wireOp",EDGE,"E16.17.39.0"),sQuery(id+"F0.wireOp",EDGE,"E16.21.39.0"),sQuery(id+"F0.wireOp",EDGE,"E16.24.39.0"),sQuery(id+"F0.wireOp",EDGE,"E16.28.39.0"),sQuery(id+"F0.wireOp",EDGE,"E16.0.40.0"),sQuery(id+"F0.wireOp",EDGE,"E16.3.40.0"),sQuery(id+"F0.wireOp",EDGE,"E16.7.40.0"),sQuery(id+"F0.wireOp",EDGE,"E16.10.40.0"),sQuery(id+"F0.wireOp",EDGE,"E16.14.40.0"),sQuery(id+"F0.wireOp",EDGE,"E16.17.40.0"),sQuery(id+"F0.wireOp",EDGE,"E16.21.40.0"),sQuery(id+"F0.wireOp",EDGE,"E16.24.40.0"),sQuery(id+"F0.wireOp",EDGE,"E16.28.40.0"),sQuery(id+"F0.wireOp",EDGE,"E16.0.41.0"),sQuery(id+"F0.wireOp",EDGE,"E16.3.41.0"),sQuery(id+"F0.wireOp",EDGE,"E16.7.41.0"),sQuery(id+"F0.wireOp",EDGE,"E16.10.41.0"),sQuery(id+"F0.wireOp",EDGE,"E16.14.41.0"),sQuery(id+"F0.wireOp",EDGE,"E16.17.41.0"),sQuery(id+"F0.wireOp",EDGE,"E16.21.41.0"),sQuery(id+"F0.wireOp",EDGE,"E16.24.41.0"),sQuery(id+"F0.wireOp",EDGE,"E16.28.41.0"),sQuery(id+"F0.wireOp",EDGE,"E16.0.42.0"),sQuery(id+"F0.wireOp",EDGE,"E16.3.42.0"),sQuery(id+"F0.wireOp",EDGE,"E16.7.42.0"),sQuery(id+"F0.wireOp",EDGE,"E16.10.42.0"),sQuery(id+"F0.wireOp",EDGE,"E16.14.42.0"),sQuery(id+"F0.wireOp",EDGE,"E16.17.42.0"),sQuery(id+"F0.wireOp",EDGE,"E16.21.42.0"),sQuery(id+"F0.wireOp",EDGE,"E16.24.42.0"),sQuery(id+"F0.wireOp",EDGE,"E16.28.42.0"),sQuery(id+"F0.wireOp",EDGE,"E16.0.43.0"),sQuery(id+"F0.wireOp",EDGE,"E16.3.43.0"),sQuery(id+"F0.wireOp",EDGE,"E16.7.43.0"),sQuery(id+"F0.wireOp",EDGE,"E16.10.43.0"),sQuery(id+"F0.wireOp",EDGE,"E16.14.43.0"),sQuery(id+"F0.wireOp",EDGE,"E16.17.43.0"),sQuery(id+"F0.wireOp",EDGE,"E16.21.43.0"),sQuery(id+"F0.wireOp",EDGE,"E16.24.43.0"),sQuery(id+"F0.wireOp",EDGE,"E16.28.43.0"),sQuery(id+"F0.wireOp",EDGE,"E16.0.44.0"),sQuery(id+"F0.wireOp",EDGE,"E16.3.44.0"),sQuery(id+"F0.wireOp",EDGE,"E16.7.44.0"),sQuery(id+"F0.wireOp",EDGE,"E16.10.44.0"),sQuery(id+"F0.wireOp",EDGE,"E16.14.44.0"),sQuery(id+"F0.wireOp",EDGE,"E16.17.44.0"),sQuery(id+"F0.wireOp",EDGE,"E16.21.44.0"),sQuery(id+"F0.wireOp",EDGE,"E16.24.44.0"),sQuery(id+"F0.wireOp",EDGE,"E16.28.44.0"),sQuery(id+"F0.wireOp",EDGE,"E16.0.45.0"),sQuery(id+"F0.wireOp",EDGE,"E16.3.45.0"),sQuery(id+"F0.wireOp",EDGE,"E16.7.45.0"),sQuery(id+"F0.wireOp",EDGE,"E16.10.45.0"),sQuery(id+"F0.wireOp",EDGE,"E16.14.45.0"),sQuery(id+"F0.wireOp",EDGE,"E16.17.45.0"),sQuery(id+"F0.wireOp",EDGE,"E16.21.45.0"),sQuery(id+"F0.wireOp",EDGE,"E16.24.45.0"),sQuery(id+"F0.wireOp",EDGE,"E16.28.45.0"),sQuery(id+"F0.wireOp",EDGE,"E16.0.46.0"),sQuery(id+"F0.wireOp",EDGE,"E16.3.46.0"),sQuery(id+"F0.wireOp",EDGE,"E16.7.46.0"),sQuery(id+"F0.wireOp",EDGE,"E16.10.46.0"),sQuery(id+"F0.wireOp",EDGE,"E16.14.46.0"),sQuery(id+"F0.wireOp",EDGE,"E16.17.46.0"),sQuery(id+"F0.wireOp",EDGE,"E16.21.46.0"),sQuery(id+"F0.wireOp",EDGE,"E16.24.46.0"),sQuery(id+"F0.wireOp",EDGE,"E16.28.46.0"),sQuery(id+"F0.wireOp",EDGE,"E16.0.47.0"),sQuery(id+"F0.wireOp",EDGE,"E16.3.47.0"),sQuery(id+"F0.wireOp",EDGE,"E16.7.47.0"),sQuery(id+"F0.wireOp",EDGE,"E16.10.47.0"),sQuery(id+"F0.wireOp",EDGE,"E16.14.47.0"),sQuery(id+"F0.wireOp",EDGE,"E16.17.47.0"),sQuery(id+"F0.wireOp",EDGE,"E16.21.47.0"),sQuery(id+"F0.wireOp",EDGE,"E16.24.47.0"),sQuery(id+"F0.wireOp",EDGE,"E16.28.47.0"),sQuery(id+"F0.wireOp",EDGE,"E16.0.48.0"),sQuery(id+"F0.wireOp",EDGE,"E16.3.48.0"),sQuery(id+"F0.wireOp",EDGE,"E16.7.48.0"),sQuery(id+"F0.wireOp",EDGE,"E16.10.48.0"),sQuery(id+"F0.wireOp",EDGE,"E16.14.48.0"),sQuery(id+"F0.wireOp",EDGE,"E16.17.48.0"),sQuery(id+"F0.wireOp",EDGE,"E16.21.48.0"),sQuery(id+"F0.wireOp",EDGE,"E16.24.48.0"),sQuery(id+"F0.wireOp",EDGE,"E16.28.48.0"),sQuery(id+"F0.wireOp",EDGE,"E16.0.49.0"),sQuery(id+"F0.wireOp",EDGE,"E16.3.49.0"),sQuery(id+"F0.wireOp",EDGE,"E16.7.49.0"),sQuery(id+"F0.wireOp",EDGE,"E16.10.49.0"),sQuery(id+"F0.wireOp",EDGE,"E16.14.49.0"),sQuery(id+"F0.wireOp",EDGE,"E16.17.49.0"),sQuery(id+"F0.wireOp",EDGE,"E16.21.49.0"),sQuery(id+"F0.wireOp",EDGE,"E16.24.49.0"),sQuery(id+"F0.wireOp",EDGE,"E16.28.49.0")])],"isStart":false});
            var sketch = newSketch(context, id + "F4", { "sketchPlane" : qUnion([Q0])});
            skLineSegment(sketch, "E26", {"start": v(0, -19.05) * mm, "end": v(0, -6.35) * mm});
            skLineSegment(sketch, "E27", {"start": v(0, -6.35) * mm, "end": v(50.8, -6.35) * mm});
            skLineSegment(sketch, "E28", {"start": v(50.8, -6.35) * mm, "end": v(50.8, -19.05) * mm});
            skLineSegment(sketch, "E29", {"start": v(762, -19.05) * mm, "end": v(762, -6.35) * mm});
            skLineSegment(sketch, "E30", {"start": v(762, -6.35) * mm, "end": v(711.2, -6.35) * mm});
            skLineSegment(sketch, "E31", {"start": v(711.2, -6.35) * mm, "end": v(711.2, -19.05) * mm});
            skSolve(sketch);
        }
        {
            var Q0;
            {var subQ0=sQuery(id+"F4.wireOp",EDGE,"E26");Q0=makeQuery(id+"F4.imprint","IMPRINT",FACE,{"disambiguationData":[TD([[makeQuery(id+"F4.imprint","IMPRINT",EDGE,{"derivedFrom":subQ0}),1.0]])]});}
            var Q1;
            {var subQ0=sQuery(id+"F4.wireOp",EDGE,"E29");Q1=makeQuery(id+"F4.imprint","IMPRINT",FACE,{"disambiguationData":[TD([[makeQuery(id+"F4.imprint","IMPRINT",EDGE,{"derivedFrom":subQ0}),-1.0]])]});}
            extrude(context, id + "F5", {"entities" : qUnion([Q0, Q1]), "operationType" : NewBodyOperationType.ADD, "depth" : 25.4 * mm});
        }
        {
            var Q0;
            Q0=makeQuery(id+"F5.opExtrude","CAP_EDGE",EDGE,{"disambiguationData":[OSD([sQuery(id+"F4.wireOp",EDGE,"E26")])],"isStart":false});
            var Q1;
            Q1=makeQuery(id+"F5.opExtrude","CAP_EDGE",EDGE,{"disambiguationData":[OSD([sQuery(id+"F4.wireOp",EDGE,"E28")])],"isStart":false});
            var Q2;
            Q2=makeQuery(id+"F5.opExtrude","CAP_EDGE",EDGE,{"disambiguationData":[OSD([sQuery(id+"F4.wireOp",EDGE,"E29")])],"isStart":false});
            var Q3;
            Q3=makeQuery(id+"F5.opExtrude","CAP_EDGE",EDGE,{"disambiguationData":[OSD([sQuery(id+"F4.wireOp",EDGE,"E31")])],"isStart":false});
            var Q4;
            Q4=makeQuery(id+"F3.opExtrude","CAP_EDGE",EDGE,{"disambiguationData":[OSD([sQuery(id+"F2.wireOp",EDGE,"E21")])],"isStart":false});
            var Q5;
            Q5=makeQuery(id+"F3.opExtrude","CAP_EDGE",EDGE,{"disambiguationData":[OSD([sQuery(id+"F2.wireOp",EDGE,"E23")])],"isStart":false});
            var Q6;
            Q6=makeQuery(id+"F3.opExtrude","CAP_EDGE",EDGE,{"disambiguationData":[OSD([sQuery(id+"F2.wireOp",EDGE,"E25")])],"isStart":false});
            var Q7;
            Q7=makeQuery(id+"F3.opExtrude","CAP_EDGE",EDGE,{"disambiguationData":[OSD([sQuery(id+"F2.wireOp",EDGE,"E24")])],"isStart":false});
            fillet(context, id + "F6", {"entities" : qUnion([Q0, Q1, Q2, Q3, Q4, Q5, Q6, Q7]), "radius" : 5.08 * mm, "tangentPropagation" : true, "allowEdgeOverflow" : false});
        }
    });
